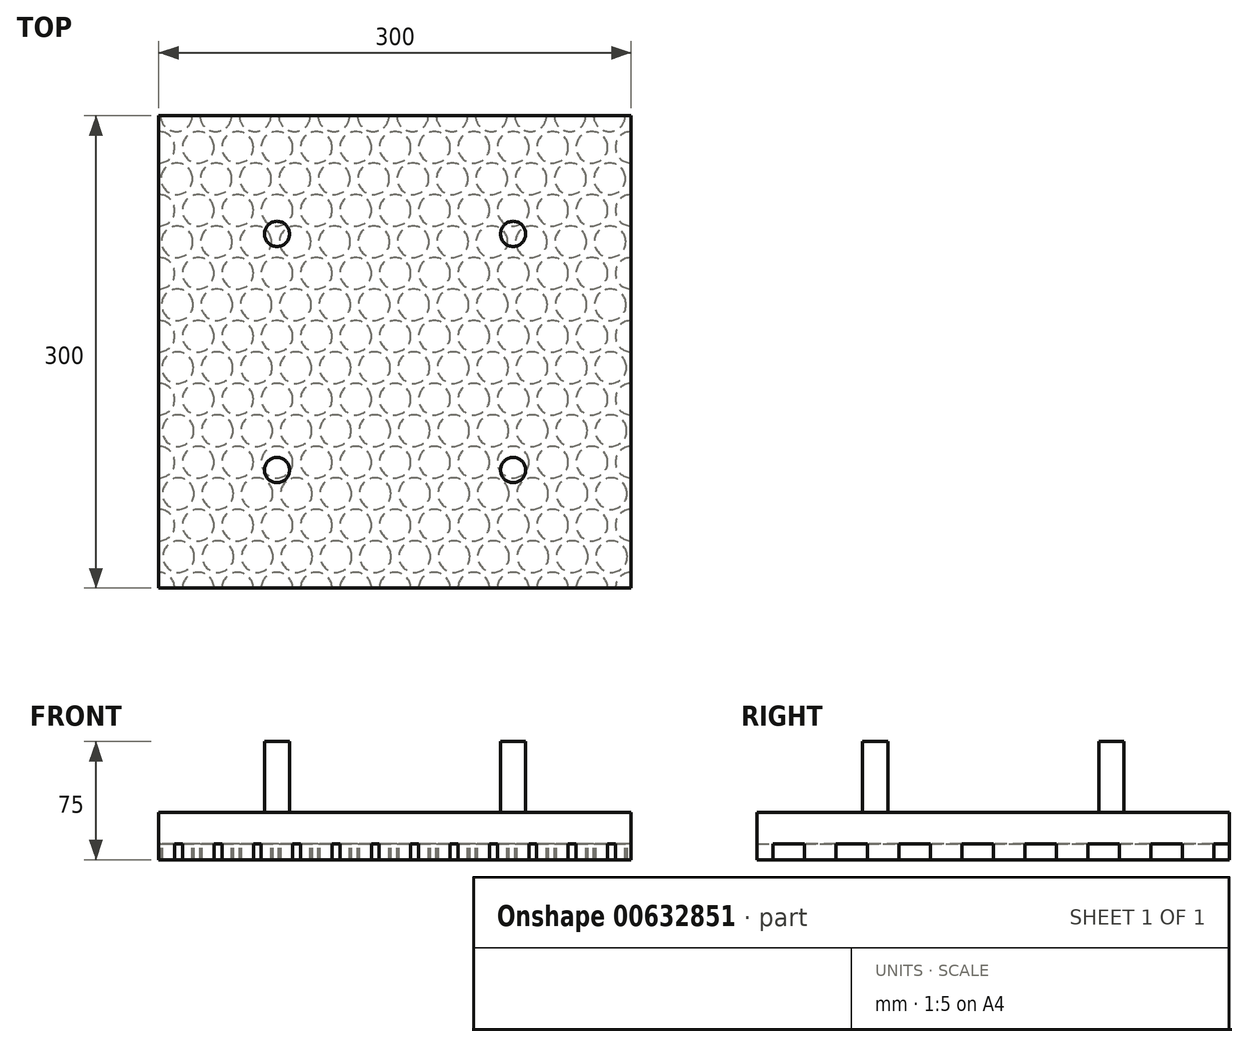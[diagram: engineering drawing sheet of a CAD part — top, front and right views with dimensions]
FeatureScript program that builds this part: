
annotation { "Feature Type Name" : "Feature", "Feature Type Description" : "" }
export const myFeature = defineFeature(function(context is Context, id is Id, definition is map)
    precondition{}
    {
        {
            var Q0;
            Q0=qCreatedBy(makeId("Top.planeOp"),FACE);
            var sketch = newSketch(context, id + "F0", { "sketchPlane" : qUnion([Q0])});
            skLineSegment(sketch, "E0.bottom", {"start": v(150, 150) * mm, "end": v(-150, 150) * mm});
            skLineSegment(sketch, "E0.top", {"start": v(150, -150) * mm, "end": v(-150, -150) * mm});
            skLineSegment(sketch, "E0.left", {"start": v(150, 150) * mm, "end": v(150, -150) * mm});
            skLineSegment(sketch, "E0.right", {"start": v(-150, 150) * mm, "end": v(-150, -150) * mm});
            skPoint(sketch, "E0.middle", {"position": v(0, 0) * mm});
            skSolve(sketch);
        }
        {
            var Q0;
            Q0 = qSketchRegion(id + "F0", true);
            extrude(context, id + "F1", {"entities" : qUnion([Q0]), "oppositeDirection" : true, "depth" : 20 * mm, "offsetDistance" : 25 * mm});
        }
        {
            var Q0;
            Q0=makeQuery(id+"F1.opExtrude","CAP_FACE",FACE,{"disambiguationData":[OSD([sQuery(id+"F0.wireOp",EDGE,"E0.bottom"),sQuery(id+"F0.wireOp",EDGE,"E0.top"),sQuery(id+"F0.wireOp",EDGE,"E0.left"),sQuery(id+"F0.wireOp",EDGE,"E0.right"),sQuery(id+"F0.wireOp",EDGE,"dzeue0mq-ryTN-MEcJ-6Cr2-TIuR5wwS6aSh"),sQuery(id+"F0.wireOp",EDGE,"DPBKmNIL-XfQO-MkqB-CjDe-bxSWGcwg6vfk"),sQuery(id+"F0.wireOp",EDGE,"v2nlQ9jK-8eDu-H6yK-LcaL-di8VHofIcNa3"),sQuery(id+"F0.wireOp",EDGE,"Z1CVN7Bm-QXrQ-2ffn-gUqZ-VcZKbfZv5ewL")])],"isStart":true});
            var sketch = newSketch(context, id + "F2", { "sketchPlane" : qUnion([Q0])});
            skCircle(sketch, "E1", {"center": v(-75, 75) * mm, "radius": 8 * mm});
            skCircle(sketch, "E2", {"center": v(75, 75) * mm, "radius": 8 * mm});
            skCircle(sketch, "E3", {"center": v(-75, -75) * mm, "radius": 8 * mm});
            skCircle(sketch, "E4", {"center": v(75, -75) * mm, "radius": 8 * mm});
            skSolve(sketch);
        }
        {
            var Q0;
            Q0 = qSketchRegion(id + "F2", true);
            extrude(context, id + "F3", {"entities" : qUnion([Q0]), "operationType" : NewBodyOperationType.ADD, "depth" : 45 * mm, "offsetDistance" : 25 * mm});
        }
        {
            var Q0;
            Q0=makeQuery(id+"F1.opExtrude","CAP_FACE",FACE,{"disambiguationData":[OSD([sQuery(id+"F0.wireOp",EDGE,"E0.bottom"),sQuery(id+"F0.wireOp",EDGE,"E0.top"),sQuery(id+"F0.wireOp",EDGE,"E0.left"),sQuery(id+"F0.wireOp",EDGE,"E0.right")])],"isStart":false});
            var sketch = newSketch(context, id + "F4", { "sketchPlane" : qUnion([Q0])});
            skCircle(sketch, "E5", {"center": v(-150, 150) * mm, "radius": 10 * mm});
            skCircle(sketch, "E6", {"center": v(-137.5, 130) * mm, "radius": 10 * mm});
            skCircle(sketch, "E7.0.1.0", {"center": v(-150, 110) * mm, "radius": 10 * mm});
            skCircle(sketch, "E7.0.2.0", {"center": v(-150, 70) * mm, "radius": 10 * mm});
            skCircle(sketch, "E7.0.3.0", {"center": v(-150, 30) * mm, "radius": 10 * mm});
            skCircle(sketch, "E7.0.4.0", {"center": v(-150, -10) * mm, "radius": 10 * mm});
            skCircle(sketch, "E7.0.5.0", {"center": v(-150, -50) * mm, "radius": 10 * mm});
            skCircle(sketch, "E7.0.6.0", {"center": v(-150, -90) * mm, "radius": 10 * mm});
            skCircle(sketch, "E7.1.0.0", {"center": v(-125, 150) * mm, "radius": 10 * mm});
            skCircle(sketch, "E7.1.1.0", {"center": v(-125, 110) * mm, "radius": 10 * mm});
            skCircle(sketch, "E7.1.2.0", {"center": v(-125, 70) * mm, "radius": 10 * mm});
            skCircle(sketch, "E7.1.3.0", {"center": v(-125, 30) * mm, "radius": 10 * mm});
            skCircle(sketch, "E7.1.4.0", {"center": v(-125, -10) * mm, "radius": 10 * mm});
            skCircle(sketch, "E7.1.5.0", {"center": v(-125, -50) * mm, "radius": 10 * mm});
            skCircle(sketch, "E7.1.6.0", {"center": v(-125, -90) * mm, "radius": 10 * mm});
            skCircle(sketch, "E7.2.0.0", {"center": v(-100, 150) * mm, "radius": 10 * mm});
            skCircle(sketch, "E7.2.1.0", {"center": v(-100, 110) * mm, "radius": 10 * mm});
            skCircle(sketch, "E7.2.2.0", {"center": v(-100, 70) * mm, "radius": 10 * mm});
            skCircle(sketch, "E7.2.3.0", {"center": v(-100, 30) * mm, "radius": 10 * mm});
            skCircle(sketch, "E7.2.4.0", {"center": v(-100, -10) * mm, "radius": 10 * mm});
            skCircle(sketch, "E7.2.5.0", {"center": v(-100, -50) * mm, "radius": 10 * mm});
            skCircle(sketch, "E7.2.6.0", {"center": v(-100, -90) * mm, "radius": 10 * mm});
            skCircle(sketch, "E7.3.0.0", {"center": v(-75, 150) * mm, "radius": 10 * mm});
            skCircle(sketch, "E7.3.1.0", {"center": v(-75, 110) * mm, "radius": 10 * mm});
            skCircle(sketch, "E7.3.2.0", {"center": v(-75, 70) * mm, "radius": 10 * mm});
            skCircle(sketch, "E7.3.3.0", {"center": v(-75, 30) * mm, "radius": 10 * mm});
            skCircle(sketch, "E7.3.4.0", {"center": v(-75, -10) * mm, "radius": 10 * mm});
            skCircle(sketch, "E7.3.5.0", {"center": v(-75, -50) * mm, "radius": 10 * mm});
            skCircle(sketch, "E7.3.6.0", {"center": v(-75, -90) * mm, "radius": 10 * mm});
            skCircle(sketch, "E7.4.0.0", {"center": v(-50, 150) * mm, "radius": 10 * mm});
            skCircle(sketch, "E7.4.1.0", {"center": v(-50, 110) * mm, "radius": 10 * mm});
            skCircle(sketch, "E7.4.2.0", {"center": v(-50, 70) * mm, "radius": 10 * mm});
            skCircle(sketch, "E7.4.3.0", {"center": v(-50, 30) * mm, "radius": 10 * mm});
            skCircle(sketch, "E7.4.4.0", {"center": v(-50, -10) * mm, "radius": 10 * mm});
            skCircle(sketch, "E7.4.5.0", {"center": v(-50, -50) * mm, "radius": 10 * mm});
            skCircle(sketch, "E7.4.6.0", {"center": v(-50, -90) * mm, "radius": 10 * mm});
            skCircle(sketch, "E7.5.0.0", {"center": v(-25, 150) * mm, "radius": 10 * mm});
            skCircle(sketch, "E7.5.1.0", {"center": v(-25, 110) * mm, "radius": 10 * mm});
            skCircle(sketch, "E7.5.2.0", {"center": v(-25, 70) * mm, "radius": 10 * mm});
            skCircle(sketch, "E7.5.3.0", {"center": v(-25, 30) * mm, "radius": 10 * mm});
            skCircle(sketch, "E7.5.4.0", {"center": v(-25, -10) * mm, "radius": 10 * mm});
            skCircle(sketch, "E7.5.5.0", {"center": v(-25, -50) * mm, "radius": 10 * mm});
            skCircle(sketch, "E7.5.6.0", {"center": v(-25, -90) * mm, "radius": 10 * mm});
            skCircle(sketch, "E7.6.0.0", {"center": v(0, 150) * mm, "radius": 10 * mm});
            skCircle(sketch, "E7.6.1.0", {"center": v(0, 110) * mm, "radius": 10 * mm});
            skCircle(sketch, "E7.6.2.0", {"center": v(0, 70) * mm, "radius": 10 * mm});
            skCircle(sketch, "E7.6.3.0", {"center": v(0, 30) * mm, "radius": 10 * mm});
            skCircle(sketch, "E7.6.4.0", {"center": v(0, -10) * mm, "radius": 10 * mm});
            skCircle(sketch, "E7.6.5.0", {"center": v(0, -50) * mm, "radius": 10 * mm});
            skCircle(sketch, "E7.6.6.0", {"center": v(0, -90) * mm, "radius": 10 * mm});
            skCircle(sketch, "E7.7.0.0", {"center": v(25, 150) * mm, "radius": 10 * mm});
            skCircle(sketch, "E7.7.1.0", {"center": v(25, 110) * mm, "radius": 10 * mm});
            skCircle(sketch, "E7.7.2.0", {"center": v(25, 70) * mm, "radius": 10 * mm});
            skCircle(sketch, "E7.7.3.0", {"center": v(25, 30) * mm, "radius": 10 * mm});
            skCircle(sketch, "E7.7.4.0", {"center": v(25, -10) * mm, "radius": 10 * mm});
            skCircle(sketch, "E7.7.5.0", {"center": v(25, -50) * mm, "radius": 10 * mm});
            skCircle(sketch, "E7.7.6.0", {"center": v(25, -90) * mm, "radius": 10 * mm});
            skCircle(sketch, "E7.8.0.0", {"center": v(50, 150) * mm, "radius": 10 * mm});
            skCircle(sketch, "E7.8.1.0", {"center": v(50, 110) * mm, "radius": 10 * mm});
            skCircle(sketch, "E7.8.2.0", {"center": v(50, 70) * mm, "radius": 10 * mm});
            skCircle(sketch, "E7.8.3.0", {"center": v(50, 30) * mm, "radius": 10 * mm});
            skCircle(sketch, "E7.8.4.0", {"center": v(50, -10) * mm, "radius": 10 * mm});
            skCircle(sketch, "E7.8.5.0", {"center": v(50, -50) * mm, "radius": 10 * mm});
            skCircle(sketch, "E7.8.6.0", {"center": v(50, -90) * mm, "radius": 10 * mm});
            skCircle(sketch, "E7.9.0.0", {"center": v(75, 150) * mm, "radius": 10 * mm});
            skCircle(sketch, "E7.9.1.0", {"center": v(75, 110) * mm, "radius": 10 * mm});
            skCircle(sketch, "E7.9.2.0", {"center": v(75, 70) * mm, "radius": 10 * mm});
            skCircle(sketch, "E7.9.3.0", {"center": v(75, 30) * mm, "radius": 10 * mm});
            skCircle(sketch, "E7.9.4.0", {"center": v(75, -10) * mm, "radius": 10 * mm});
            skCircle(sketch, "E7.9.5.0", {"center": v(75, -50) * mm, "radius": 10 * mm});
            skCircle(sketch, "E7.9.6.0", {"center": v(75, -90) * mm, "radius": 10 * mm});
            skLineSegment(sketch, "E7.direction1", {"start": v(-150, 150) * mm, "end": v(-125, 150) * mm, "construction": true});
            skLineSegment(sketch, "E7.direction2", {"start": v(-150, 150) * mm, "end": v(-150, 110) * mm, "construction": true});
            skCircle(sketch, "E8.0.1.0", {"center": v(-137.7, 90) * mm, "radius": 10 * mm});
            skCircle(sketch, "E8.0.2.0", {"center": v(-137.88, 50) * mm, "radius": 10 * mm});
            skCircle(sketch, "E8.0.3.0", {"center": v(-138.07, 10) * mm, "radius": 10 * mm});
            skCircle(sketch, "E8.0.4.0", {"center": v(-138.27, -30) * mm, "radius": 10 * mm});
            skCircle(sketch, "E8.0.5.0", {"center": v(-138.46, -70) * mm, "radius": 10 * mm});
            skCircle(sketch, "E8.0.6.0", {"center": v(-138.65, -110) * mm, "radius": 10 * mm});
            skCircle(sketch, "E8.0.7.0", {"center": v(-138.84, -150) * mm, "radius": 10 * mm});
            skCircle(sketch, "E8.1.0.0", {"center": v(-112.5, 130) * mm, "radius": 10 * mm});
            skCircle(sketch, "E8.1.1.0", {"center": v(-112.7, 90) * mm, "radius": 10 * mm});
            skCircle(sketch, "E8.1.2.0", {"center": v(-112.88, 50) * mm, "radius": 10 * mm});
            skCircle(sketch, "E8.1.3.0", {"center": v(-113.07, 10) * mm, "radius": 10 * mm});
            skCircle(sketch, "E8.1.4.0", {"center": v(-113.27, -30) * mm, "radius": 10 * mm});
            skCircle(sketch, "E8.1.5.0", {"center": v(-113.46, -70) * mm, "radius": 10 * mm});
            skCircle(sketch, "E8.1.6.0", {"center": v(-113.65, -110) * mm, "radius": 10 * mm});
            skCircle(sketch, "E8.1.7.0", {"center": v(-113.84, -150) * mm, "radius": 10 * mm});
            skCircle(sketch, "E8.2.0.0", {"center": v(-87.5, 130) * mm, "radius": 10 * mm});
            skCircle(sketch, "E8.2.1.0", {"center": v(-87.7, 90) * mm, "radius": 10 * mm});
            skCircle(sketch, "E8.2.2.0", {"center": v(-87.88, 50) * mm, "radius": 10 * mm});
            skCircle(sketch, "E8.2.3.0", {"center": v(-88.07, 10) * mm, "radius": 10 * mm});
            skCircle(sketch, "E8.2.4.0", {"center": v(-88.27, -30) * mm, "radius": 10 * mm});
            skCircle(sketch, "E8.2.5.0", {"center": v(-88.46, -70) * mm, "radius": 10 * mm});
            skCircle(sketch, "E8.2.6.0", {"center": v(-88.65, -110) * mm, "radius": 10 * mm});
            skCircle(sketch, "E8.2.7.0", {"center": v(-88.84, -150) * mm, "radius": 10 * mm});
            skCircle(sketch, "E8.3.0.0", {"center": v(-62.5, 130) * mm, "radius": 10 * mm});
            skCircle(sketch, "E8.3.1.0", {"center": v(-62.7, 90) * mm, "radius": 10 * mm});
            skCircle(sketch, "E8.3.2.0", {"center": v(-62.88, 50) * mm, "radius": 10 * mm});
            skCircle(sketch, "E8.3.3.0", {"center": v(-63.07, 10) * mm, "radius": 10 * mm});
            skCircle(sketch, "E8.3.4.0", {"center": v(-63.27, -30) * mm, "radius": 10 * mm});
            skCircle(sketch, "E8.3.5.0", {"center": v(-63.46, -70) * mm, "radius": 10 * mm});
            skCircle(sketch, "E8.3.6.0", {"center": v(-63.65, -110) * mm, "radius": 10 * mm});
            skCircle(sketch, "E8.3.7.0", {"center": v(-63.84, -150) * mm, "radius": 10 * mm});
            skCircle(sketch, "E8.4.0.0", {"center": v(-37.5, 130) * mm, "radius": 10 * mm});
            skCircle(sketch, "E8.4.1.0", {"center": v(-37.7, 90) * mm, "radius": 10 * mm});
            skCircle(sketch, "E8.4.2.0", {"center": v(-37.88, 50) * mm, "radius": 10 * mm});
            skCircle(sketch, "E8.4.3.0", {"center": v(-38.07, 10) * mm, "radius": 10 * mm});
            skCircle(sketch, "E8.4.4.0", {"center": v(-38.27, -30) * mm, "radius": 10 * mm});
            skCircle(sketch, "E8.4.5.0", {"center": v(-38.46, -70) * mm, "radius": 10 * mm});
            skCircle(sketch, "E8.4.6.0", {"center": v(-38.65, -110) * mm, "radius": 10 * mm});
            skCircle(sketch, "E8.4.7.0", {"center": v(-38.84, -150) * mm, "radius": 10 * mm});
            skCircle(sketch, "E8.5.0.0", {"center": v(-12.5, 130) * mm, "radius": 10 * mm});
            skCircle(sketch, "E8.5.1.0", {"center": v(-12.7, 90) * mm, "radius": 10 * mm});
            skCircle(sketch, "E8.5.2.0", {"center": v(-12.88, 50) * mm, "radius": 10 * mm});
            skCircle(sketch, "E8.5.3.0", {"center": v(-13.07, 10) * mm, "radius": 10 * mm});
            skCircle(sketch, "E8.5.4.0", {"center": v(-13.27, -30) * mm, "radius": 10 * mm});
            skCircle(sketch, "E8.5.5.0", {"center": v(-13.46, -70) * mm, "radius": 10 * mm});
            skCircle(sketch, "E8.5.6.0", {"center": v(-13.65, -110) * mm, "radius": 10 * mm});
            skCircle(sketch, "E8.5.7.0", {"center": v(-13.84, -150) * mm, "radius": 10 * mm});
            skCircle(sketch, "E8.6.0.0", {"center": v(12.5, 130) * mm, "radius": 10 * mm});
            skCircle(sketch, "E8.6.1.0", {"center": v(12.3, 90) * mm, "radius": 10 * mm});
            skCircle(sketch, "E8.6.2.0", {"center": v(12.12, 50) * mm, "radius": 10 * mm});
            skCircle(sketch, "E8.6.3.0", {"center": v(11.93, 10) * mm, "radius": 10 * mm});
            skCircle(sketch, "E8.6.4.0", {"center": v(11.73, -30) * mm, "radius": 10 * mm});
            skCircle(sketch, "E8.6.5.0", {"center": v(11.54, -70) * mm, "radius": 10 * mm});
            skCircle(sketch, "E8.6.6.0", {"center": v(11.35, -110) * mm, "radius": 10 * mm});
            skCircle(sketch, "E8.6.7.0", {"center": v(11.16, -150) * mm, "radius": 10 * mm});
            skCircle(sketch, "E8.7.0.0", {"center": v(37.5, 130) * mm, "radius": 10 * mm});
            skCircle(sketch, "E8.7.1.0", {"center": v(37.3, 90) * mm, "radius": 10 * mm});
            skCircle(sketch, "E8.7.2.0", {"center": v(37.12, 50) * mm, "radius": 10 * mm});
            skCircle(sketch, "E8.7.3.0", {"center": v(36.93, 10) * mm, "radius": 10 * mm});
            skCircle(sketch, "E8.7.4.0", {"center": v(36.73, -30) * mm, "radius": 10 * mm});
            skCircle(sketch, "E8.7.5.0", {"center": v(36.54, -70) * mm, "radius": 10 * mm});
            skCircle(sketch, "E8.7.6.0", {"center": v(36.35, -110) * mm, "radius": 10 * mm});
            skCircle(sketch, "E8.7.7.0", {"center": v(36.16, -150) * mm, "radius": 10 * mm});
            skCircle(sketch, "E8.8.0.0", {"center": v(62.5, 130) * mm, "radius": 10 * mm});
            skCircle(sketch, "E8.8.1.0", {"center": v(62.3, 90) * mm, "radius": 10 * mm});
            skCircle(sketch, "E8.8.2.0", {"center": v(62.12, 50) * mm, "radius": 10 * mm});
            skCircle(sketch, "E8.8.3.0", {"center": v(61.93, 10) * mm, "radius": 10 * mm});
            skCircle(sketch, "E8.8.4.0", {"center": v(61.73, -30) * mm, "radius": 10 * mm});
            skCircle(sketch, "E8.8.5.0", {"center": v(61.54, -70) * mm, "radius": 10 * mm});
            skCircle(sketch, "E8.8.6.0", {"center": v(61.35, -110) * mm, "radius": 10 * mm});
            skCircle(sketch, "E8.8.7.0", {"center": v(61.16, -150) * mm, "radius": 10 * mm});
            skCircle(sketch, "E8.9.0.0", {"center": v(87.5, 130) * mm, "radius": 10 * mm});
            skCircle(sketch, "E8.9.1.0", {"center": v(87.3, 90) * mm, "radius": 10 * mm});
            skCircle(sketch, "E8.9.2.0", {"center": v(87.12, 50) * mm, "radius": 10 * mm});
            skCircle(sketch, "E8.9.3.0", {"center": v(86.93, 10) * mm, "radius": 10 * mm});
            skCircle(sketch, "E8.9.4.0", {"center": v(86.73, -30) * mm, "radius": 10 * mm});
            skCircle(sketch, "E8.9.5.0", {"center": v(86.54, -70) * mm, "radius": 10 * mm});
            skCircle(sketch, "E8.9.6.0", {"center": v(86.35, -110) * mm, "radius": 10 * mm});
            skCircle(sketch, "E8.9.7.0", {"center": v(86.16, -150) * mm, "radius": 10 * mm});
            skCircle(sketch, "E8.10.0.0", {"center": v(112.5, 130) * mm, "radius": 10 * mm});
            skCircle(sketch, "E8.10.1.0", {"center": v(112.3, 90) * mm, "radius": 10 * mm});
            skCircle(sketch, "E8.10.2.0", {"center": v(112.12, 50) * mm, "radius": 10 * mm});
            skCircle(sketch, "E8.10.3.0", {"center": v(111.93, 10) * mm, "radius": 10 * mm});
            skCircle(sketch, "E8.10.4.0", {"center": v(111.73, -30) * mm, "radius": 10 * mm});
            skCircle(sketch, "E8.10.5.0", {"center": v(111.54, -70) * mm, "radius": 10 * mm});
            skCircle(sketch, "E8.10.6.0", {"center": v(111.35, -110) * mm, "radius": 10 * mm});
            skCircle(sketch, "E8.10.7.0", {"center": v(111.16, -150) * mm, "radius": 10 * mm});
            skCircle(sketch, "E8.11.0.0", {"center": v(137.5, 130) * mm, "radius": 10 * mm});
            skCircle(sketch, "E8.11.1.0", {"center": v(137.3, 90) * mm, "radius": 10 * mm});
            skCircle(sketch, "E8.11.2.0", {"center": v(137.12, 50) * mm, "radius": 10 * mm});
            skCircle(sketch, "E8.11.3.0", {"center": v(136.93, 10) * mm, "radius": 10 * mm});
            skCircle(sketch, "E8.11.4.0", {"center": v(136.73, -30) * mm, "radius": 10 * mm});
            skCircle(sketch, "E8.11.5.0", {"center": v(136.54, -70) * mm, "radius": 10 * mm});
            skCircle(sketch, "E8.11.6.0", {"center": v(136.35, -110) * mm, "radius": 10 * mm});
            skCircle(sketch, "E8.11.7.0", {"center": v(136.16, -150) * mm, "radius": 10 * mm});
            skLineSegment(sketch, "E8.direction1", {"start": v(-137.5, 130) * mm, "end": v(-112.5, 130) * mm, "construction": true});
            skLineSegment(sketch, "E8.direction2", {"start": v(-137.5, 130) * mm, "end": v(-137.7, 90) * mm, "construction": true});
            skCircle(sketch, "E9.0.0.7", {"center": v(-150, -130) * mm, "radius": 10 * mm});
            skCircle(sketch, "E9.0.1.7", {"center": v(-125, -130) * mm, "radius": 10 * mm});
            skCircle(sketch, "E9.0.2.7", {"center": v(-100, -130) * mm, "radius": 10 * mm});
            skCircle(sketch, "E9.0.3.7", {"center": v(-75, -130) * mm, "radius": 10 * mm});
            skCircle(sketch, "E9.0.4.7", {"center": v(-50, -130) * mm, "radius": 10 * mm});
            skCircle(sketch, "E9.0.5.7", {"center": v(-25, -130) * mm, "radius": 10 * mm});
            skCircle(sketch, "E9.0.6.7", {"center": v(0, -130) * mm, "radius": 10 * mm});
            skCircle(sketch, "E9.0.7.7", {"center": v(25, -130) * mm, "radius": 10 * mm});
            skCircle(sketch, "E9.0.8.7", {"center": v(50, -130) * mm, "radius": 10 * mm});
            skCircle(sketch, "E9.0.9.7", {"center": v(75, -130) * mm, "radius": 10 * mm});
            skCircle(sketch, "E10.0.10.0", {"center": v(100, 150) * mm, "radius": 10 * mm});
            skCircle(sketch, "E10.0.10.1", {"center": v(100, 110) * mm, "radius": 10 * mm});
            skCircle(sketch, "E10.0.10.2", {"center": v(100, 70) * mm, "radius": 10 * mm});
            skCircle(sketch, "E10.0.10.3", {"center": v(100, 30) * mm, "radius": 10 * mm});
            skCircle(sketch, "E10.0.10.4", {"center": v(100, -10) * mm, "radius": 10 * mm});
            skCircle(sketch, "E10.0.10.5", {"center": v(100, -50) * mm, "radius": 10 * mm});
            skCircle(sketch, "E10.0.10.6", {"center": v(100, -90) * mm, "radius": 10 * mm});
            skCircle(sketch, "E10.0.10.7", {"center": v(100, -130) * mm, "radius": 10 * mm});
            skCircle(sketch, "E10.0.11.0", {"center": v(125, 150) * mm, "radius": 10 * mm});
            skCircle(sketch, "E10.0.11.1", {"center": v(125, 110) * mm, "radius": 10 * mm});
            skCircle(sketch, "E10.0.11.2", {"center": v(125, 70) * mm, "radius": 10 * mm});
            skCircle(sketch, "E10.0.11.3", {"center": v(125, 30) * mm, "radius": 10 * mm});
            skCircle(sketch, "E10.0.11.4", {"center": v(125, -10) * mm, "radius": 10 * mm});
            skCircle(sketch, "E10.0.11.5", {"center": v(125, -50) * mm, "radius": 10 * mm});
            skCircle(sketch, "E10.0.11.6", {"center": v(125, -90) * mm, "radius": 10 * mm});
            skCircle(sketch, "E10.0.11.7", {"center": v(125, -130) * mm, "radius": 10 * mm});
            skCircle(sketch, "E11.0.12.0", {"center": v(150, 150) * mm, "radius": 10 * mm});
            skCircle(sketch, "E11.0.12.1", {"center": v(150, 110) * mm, "radius": 10 * mm});
            skCircle(sketch, "E11.0.12.2", {"center": v(150, 70) * mm, "radius": 10 * mm});
            skCircle(sketch, "E11.0.12.3", {"center": v(150, 30) * mm, "radius": 10 * mm});
            skCircle(sketch, "E11.0.12.4", {"center": v(150, -10) * mm, "radius": 10 * mm});
            skCircle(sketch, "E11.0.12.5", {"center": v(150, -50) * mm, "radius": 10 * mm});
            skCircle(sketch, "E11.0.12.6", {"center": v(150, -90) * mm, "radius": 10 * mm});
            skCircle(sketch, "E11.0.12.7", {"center": v(150, -130) * mm, "radius": 10 * mm});
            skSolve(sketch);
        }
        {
            var Q0;
            Q0=makeQuery(id+"F4.imprint","IMPRINT",FACE,{"disambiguationData":[TD([[makeQuery(id+"F4.imprint","IMPRINT",EDGE,{"derivedFrom":sQuery(id+"F4.wireOp",EDGE,"E6")}),1.0]])]});
            var Q1;
            Q1=makeQuery(id+"F4.imprint","IMPRINT",FACE,{"disambiguationData":[TD([[makeQuery(id+"F4.imprint","IMPRINT",EDGE,{"derivedFrom":sQuery(id+"F4.wireOp",EDGE,"E7.1.1.0")}),1.0]])]});
            var Q2;
            Q2=makeQuery(id+"F4.imprint","IMPRINT",FACE,{"disambiguationData":[TD([[makeQuery(id+"F4.imprint","IMPRINT",EDGE,{"derivedFrom":sQuery(id+"F4.wireOp",EDGE,"E7.1.2.0")}),1.0]])]});
            var Q3;
            Q3=makeQuery(id+"F4.imprint","IMPRINT",FACE,{"disambiguationData":[TD([[makeQuery(id+"F4.imprint","IMPRINT",EDGE,{"derivedFrom":sQuery(id+"F4.wireOp",EDGE,"E7.1.3.0")}),1.0]])]});
            var Q4;
            Q4=makeQuery(id+"F4.imprint","IMPRINT",FACE,{"disambiguationData":[TD([[makeQuery(id+"F4.imprint","IMPRINT",EDGE,{"derivedFrom":sQuery(id+"F4.wireOp",EDGE,"E7.1.4.0")}),1.0]])]});
            var Q5;
            Q5=makeQuery(id+"F4.imprint","IMPRINT",FACE,{"disambiguationData":[TD([[makeQuery(id+"F4.imprint","IMPRINT",EDGE,{"derivedFrom":sQuery(id+"F4.wireOp",EDGE,"E7.1.5.0")}),1.0]])]});
            var Q6;
            Q6=makeQuery(id+"F4.imprint","IMPRINT",FACE,{"disambiguationData":[TD([[makeQuery(id+"F4.imprint","IMPRINT",EDGE,{"derivedFrom":sQuery(id+"F4.wireOp",EDGE,"E7.1.6.0")}),1.0]])]});
            var Q7;
            Q7=makeQuery(id+"F4.imprint","IMPRINT",FACE,{"disambiguationData":[TD([[makeQuery(id+"F4.imprint","IMPRINT",EDGE,{"derivedFrom":sQuery(id+"F4.wireOp",EDGE,"E7.2.1.0")}),1.0]])]});
            var Q8;
            Q8=makeQuery(id+"F4.imprint","IMPRINT",FACE,{"disambiguationData":[TD([[makeQuery(id+"F4.imprint","IMPRINT",EDGE,{"derivedFrom":sQuery(id+"F4.wireOp",EDGE,"E7.2.2.0")}),1.0]])]});
            var Q9;
            Q9=makeQuery(id+"F4.imprint","IMPRINT",FACE,{"disambiguationData":[TD([[makeQuery(id+"F4.imprint","IMPRINT",EDGE,{"derivedFrom":sQuery(id+"F4.wireOp",EDGE,"E7.2.3.0")}),1.0]])]});
            var Q10;
            Q10=makeQuery(id+"F4.imprint","IMPRINT",FACE,{"disambiguationData":[TD([[makeQuery(id+"F4.imprint","IMPRINT",EDGE,{"derivedFrom":sQuery(id+"F4.wireOp",EDGE,"E7.2.4.0")}),1.0]])]});
            var Q11;
            Q11=makeQuery(id+"F4.imprint","IMPRINT",FACE,{"disambiguationData":[TD([[makeQuery(id+"F4.imprint","IMPRINT",EDGE,{"derivedFrom":sQuery(id+"F4.wireOp",EDGE,"E7.2.5.0")}),1.0]])]});
            var Q12;
            Q12=makeQuery(id+"F4.imprint","IMPRINT",FACE,{"disambiguationData":[TD([[makeQuery(id+"F4.imprint","IMPRINT",EDGE,{"derivedFrom":sQuery(id+"F4.wireOp",EDGE,"E7.2.6.0")}),1.0]])]});
            var Q13;
            Q13=makeQuery(id+"F4.imprint","IMPRINT",FACE,{"disambiguationData":[TD([[makeQuery(id+"F4.imprint","IMPRINT",EDGE,{"derivedFrom":sQuery(id+"F4.wireOp",EDGE,"E7.3.1.0")}),1.0]])]});
            var Q14;
            Q14=makeQuery(id+"F4.imprint","IMPRINT",FACE,{"disambiguationData":[TD([[makeQuery(id+"F4.imprint","IMPRINT",EDGE,{"derivedFrom":sQuery(id+"F4.wireOp",EDGE,"E7.3.2.0")}),1.0]])]});
            var Q15;
            Q15=makeQuery(id+"F4.imprint","IMPRINT",FACE,{"disambiguationData":[TD([[makeQuery(id+"F4.imprint","IMPRINT",EDGE,{"derivedFrom":sQuery(id+"F4.wireOp",EDGE,"E7.3.3.0")}),1.0]])]});
            var Q16;
            Q16=makeQuery(id+"F4.imprint","IMPRINT",FACE,{"disambiguationData":[TD([[makeQuery(id+"F4.imprint","IMPRINT",EDGE,{"derivedFrom":sQuery(id+"F4.wireOp",EDGE,"E7.3.4.0")}),1.0]])]});
            var Q17;
            Q17=makeQuery(id+"F4.imprint","IMPRINT",FACE,{"disambiguationData":[TD([[makeQuery(id+"F4.imprint","IMPRINT",EDGE,{"derivedFrom":sQuery(id+"F4.wireOp",EDGE,"E7.3.5.0")}),1.0]])]});
            var Q18;
            Q18=makeQuery(id+"F4.imprint","IMPRINT",FACE,{"disambiguationData":[TD([[makeQuery(id+"F4.imprint","IMPRINT",EDGE,{"derivedFrom":sQuery(id+"F4.wireOp",EDGE,"E7.3.6.0")}),1.0]])]});
            var Q19;
            Q19=makeQuery(id+"F4.imprint","IMPRINT",FACE,{"disambiguationData":[TD([[makeQuery(id+"F4.imprint","IMPRINT",EDGE,{"derivedFrom":sQuery(id+"F4.wireOp",EDGE,"E7.4.1.0")}),1.0]])]});
            var Q20;
            Q20=makeQuery(id+"F4.imprint","IMPRINT",FACE,{"disambiguationData":[TD([[makeQuery(id+"F4.imprint","IMPRINT",EDGE,{"derivedFrom":sQuery(id+"F4.wireOp",EDGE,"E7.4.2.0")}),1.0]])]});
            var Q21;
            Q21=makeQuery(id+"F4.imprint","IMPRINT",FACE,{"disambiguationData":[TD([[makeQuery(id+"F4.imprint","IMPRINT",EDGE,{"derivedFrom":sQuery(id+"F4.wireOp",EDGE,"E7.4.3.0")}),1.0]])]});
            var Q22;
            Q22=makeQuery(id+"F4.imprint","IMPRINT",FACE,{"disambiguationData":[TD([[makeQuery(id+"F4.imprint","IMPRINT",EDGE,{"derivedFrom":sQuery(id+"F4.wireOp",EDGE,"E7.4.4.0")}),1.0]])]});
            var Q23;
            Q23=makeQuery(id+"F4.imprint","IMPRINT",FACE,{"disambiguationData":[TD([[makeQuery(id+"F4.imprint","IMPRINT",EDGE,{"derivedFrom":sQuery(id+"F4.wireOp",EDGE,"E7.4.5.0")}),1.0]])]});
            var Q24;
            Q24=makeQuery(id+"F4.imprint","IMPRINT",FACE,{"disambiguationData":[TD([[makeQuery(id+"F4.imprint","IMPRINT",EDGE,{"derivedFrom":sQuery(id+"F4.wireOp",EDGE,"E7.4.6.0")}),1.0]])]});
            var Q25;
            Q25=makeQuery(id+"F4.imprint","IMPRINT",FACE,{"disambiguationData":[TD([[makeQuery(id+"F4.imprint","IMPRINT",EDGE,{"derivedFrom":sQuery(id+"F4.wireOp",EDGE,"E7.5.1.0")}),1.0]])]});
            var Q26;
            Q26=makeQuery(id+"F4.imprint","IMPRINT",FACE,{"disambiguationData":[TD([[makeQuery(id+"F4.imprint","IMPRINT",EDGE,{"derivedFrom":sQuery(id+"F4.wireOp",EDGE,"E7.5.2.0")}),1.0]])]});
            var Q27;
            Q27=makeQuery(id+"F4.imprint","IMPRINT",FACE,{"disambiguationData":[TD([[makeQuery(id+"F4.imprint","IMPRINT",EDGE,{"derivedFrom":sQuery(id+"F4.wireOp",EDGE,"E7.5.3.0")}),1.0]])]});
            var Q28;
            Q28=makeQuery(id+"F4.imprint","IMPRINT",FACE,{"disambiguationData":[TD([[makeQuery(id+"F4.imprint","IMPRINT",EDGE,{"derivedFrom":sQuery(id+"F4.wireOp",EDGE,"E7.5.4.0")}),1.0]])]});
            var Q29;
            Q29=makeQuery(id+"F4.imprint","IMPRINT",FACE,{"disambiguationData":[TD([[makeQuery(id+"F4.imprint","IMPRINT",EDGE,{"derivedFrom":sQuery(id+"F4.wireOp",EDGE,"E7.5.5.0")}),1.0]])]});
            var Q30;
            Q30=makeQuery(id+"F4.imprint","IMPRINT",FACE,{"disambiguationData":[TD([[makeQuery(id+"F4.imprint","IMPRINT",EDGE,{"derivedFrom":sQuery(id+"F4.wireOp",EDGE,"E7.5.6.0")}),1.0]])]});
            var Q31;
            Q31=makeQuery(id+"F4.imprint","IMPRINT",FACE,{"disambiguationData":[TD([[makeQuery(id+"F4.imprint","IMPRINT",EDGE,{"derivedFrom":sQuery(id+"F4.wireOp",EDGE,"E7.6.1.0")}),1.0]])]});
            var Q32;
            Q32=makeQuery(id+"F4.imprint","IMPRINT",FACE,{"disambiguationData":[TD([[makeQuery(id+"F4.imprint","IMPRINT",EDGE,{"derivedFrom":sQuery(id+"F4.wireOp",EDGE,"E7.6.2.0")}),1.0]])]});
            var Q33;
            Q33=makeQuery(id+"F4.imprint","IMPRINT",FACE,{"disambiguationData":[TD([[makeQuery(id+"F4.imprint","IMPRINT",EDGE,{"derivedFrom":sQuery(id+"F4.wireOp",EDGE,"E7.6.3.0")}),1.0]])]});
            var Q34;
            Q34=makeQuery(id+"F4.imprint","IMPRINT",FACE,{"disambiguationData":[TD([[makeQuery(id+"F4.imprint","IMPRINT",EDGE,{"derivedFrom":sQuery(id+"F4.wireOp",EDGE,"E7.6.4.0")}),1.0]])]});
            var Q35;
            Q35=makeQuery(id+"F4.imprint","IMPRINT",FACE,{"disambiguationData":[TD([[makeQuery(id+"F4.imprint","IMPRINT",EDGE,{"derivedFrom":sQuery(id+"F4.wireOp",EDGE,"E7.6.5.0")}),1.0]])]});
            var Q36;
            Q36=makeQuery(id+"F4.imprint","IMPRINT",FACE,{"disambiguationData":[TD([[makeQuery(id+"F4.imprint","IMPRINT",EDGE,{"derivedFrom":sQuery(id+"F4.wireOp",EDGE,"E7.6.6.0")}),1.0]])]});
            var Q37;
            Q37=makeQuery(id+"F4.imprint","IMPRINT",FACE,{"disambiguationData":[TD([[makeQuery(id+"F4.imprint","IMPRINT",EDGE,{"derivedFrom":sQuery(id+"F4.wireOp",EDGE,"E7.7.1.0")}),1.0]])]});
            var Q38;
            Q38=makeQuery(id+"F4.imprint","IMPRINT",FACE,{"disambiguationData":[TD([[makeQuery(id+"F4.imprint","IMPRINT",EDGE,{"derivedFrom":sQuery(id+"F4.wireOp",EDGE,"E7.7.2.0")}),1.0]])]});
            var Q39;
            Q39=makeQuery(id+"F4.imprint","IMPRINT",FACE,{"disambiguationData":[TD([[makeQuery(id+"F4.imprint","IMPRINT",EDGE,{"derivedFrom":sQuery(id+"F4.wireOp",EDGE,"E7.7.3.0")}),1.0]])]});
            var Q40;
            Q40=makeQuery(id+"F4.imprint","IMPRINT",FACE,{"disambiguationData":[TD([[makeQuery(id+"F4.imprint","IMPRINT",EDGE,{"derivedFrom":sQuery(id+"F4.wireOp",EDGE,"E7.7.4.0")}),1.0]])]});
            var Q41;
            Q41=makeQuery(id+"F4.imprint","IMPRINT",FACE,{"disambiguationData":[TD([[makeQuery(id+"F4.imprint","IMPRINT",EDGE,{"derivedFrom":sQuery(id+"F4.wireOp",EDGE,"E7.7.5.0")}),1.0]])]});
            var Q42;
            Q42=makeQuery(id+"F4.imprint","IMPRINT",FACE,{"disambiguationData":[TD([[makeQuery(id+"F4.imprint","IMPRINT",EDGE,{"derivedFrom":sQuery(id+"F4.wireOp",EDGE,"E7.7.6.0")}),1.0]])]});
            var Q43;
            Q43=makeQuery(id+"F4.imprint","IMPRINT",FACE,{"disambiguationData":[TD([[makeQuery(id+"F4.imprint","IMPRINT",EDGE,{"derivedFrom":sQuery(id+"F4.wireOp",EDGE,"E7.8.1.0")}),1.0]])]});
            var Q44;
            Q44=makeQuery(id+"F4.imprint","IMPRINT",FACE,{"disambiguationData":[TD([[makeQuery(id+"F4.imprint","IMPRINT",EDGE,{"derivedFrom":sQuery(id+"F4.wireOp",EDGE,"E7.8.2.0")}),1.0]])]});
            var Q45;
            Q45=makeQuery(id+"F4.imprint","IMPRINT",FACE,{"disambiguationData":[TD([[makeQuery(id+"F4.imprint","IMPRINT",EDGE,{"derivedFrom":sQuery(id+"F4.wireOp",EDGE,"E7.8.3.0")}),1.0]])]});
            var Q46;
            Q46=makeQuery(id+"F4.imprint","IMPRINT",FACE,{"disambiguationData":[TD([[makeQuery(id+"F4.imprint","IMPRINT",EDGE,{"derivedFrom":sQuery(id+"F4.wireOp",EDGE,"E7.8.4.0")}),1.0]])]});
            var Q47;
            Q47=makeQuery(id+"F4.imprint","IMPRINT",FACE,{"disambiguationData":[TD([[makeQuery(id+"F4.imprint","IMPRINT",EDGE,{"derivedFrom":sQuery(id+"F4.wireOp",EDGE,"E7.8.5.0")}),1.0]])]});
            var Q48;
            Q48=makeQuery(id+"F4.imprint","IMPRINT",FACE,{"disambiguationData":[TD([[makeQuery(id+"F4.imprint","IMPRINT",EDGE,{"derivedFrom":sQuery(id+"F4.wireOp",EDGE,"E7.8.6.0")}),1.0]])]});
            var Q49;
            Q49=makeQuery(id+"F4.imprint","IMPRINT",FACE,{"disambiguationData":[TD([[makeQuery(id+"F4.imprint","IMPRINT",EDGE,{"derivedFrom":sQuery(id+"F4.wireOp",EDGE,"E7.9.1.0")}),1.0]])]});
            var Q50;
            Q50=makeQuery(id+"F4.imprint","IMPRINT",FACE,{"disambiguationData":[TD([[makeQuery(id+"F4.imprint","IMPRINT",EDGE,{"derivedFrom":sQuery(id+"F4.wireOp",EDGE,"E7.9.2.0")}),1.0]])]});
            var Q51;
            Q51=makeQuery(id+"F4.imprint","IMPRINT",FACE,{"disambiguationData":[TD([[makeQuery(id+"F4.imprint","IMPRINT",EDGE,{"derivedFrom":sQuery(id+"F4.wireOp",EDGE,"E7.9.3.0")}),1.0]])]});
            var Q52;
            Q52=makeQuery(id+"F4.imprint","IMPRINT",FACE,{"disambiguationData":[TD([[makeQuery(id+"F4.imprint","IMPRINT",EDGE,{"derivedFrom":sQuery(id+"F4.wireOp",EDGE,"E7.9.4.0")}),1.0]])]});
            var Q53;
            Q53=makeQuery(id+"F4.imprint","IMPRINT",FACE,{"disambiguationData":[TD([[makeQuery(id+"F4.imprint","IMPRINT",EDGE,{"derivedFrom":sQuery(id+"F4.wireOp",EDGE,"E7.9.5.0")}),1.0]])]});
            var Q54;
            Q54=makeQuery(id+"F4.imprint","IMPRINT",FACE,{"disambiguationData":[TD([[makeQuery(id+"F4.imprint","IMPRINT",EDGE,{"derivedFrom":sQuery(id+"F4.wireOp",EDGE,"E7.9.6.0")}),1.0]])]});
            var Q55;
            Q55=makeQuery(id+"F4.imprint","IMPRINT",FACE,{"disambiguationData":[TD([[makeQuery(id+"F4.imprint","IMPRINT",EDGE,{"derivedFrom":sQuery(id+"F4.wireOp",EDGE,"E8.0.1.0")}),1.0]])]});
            var Q56;
            Q56=makeQuery(id+"F4.imprint","IMPRINT",FACE,{"disambiguationData":[TD([[makeQuery(id+"F4.imprint","IMPRINT",EDGE,{"derivedFrom":sQuery(id+"F4.wireOp",EDGE,"E8.0.2.0")}),1.0]])]});
            var Q57;
            Q57=makeQuery(id+"F4.imprint","IMPRINT",FACE,{"disambiguationData":[TD([[makeQuery(id+"F4.imprint","IMPRINT",EDGE,{"derivedFrom":sQuery(id+"F4.wireOp",EDGE,"E8.0.3.0")}),1.0]])]});
            var Q58;
            Q58=makeQuery(id+"F4.imprint","IMPRINT",FACE,{"disambiguationData":[TD([[makeQuery(id+"F4.imprint","IMPRINT",EDGE,{"derivedFrom":sQuery(id+"F4.wireOp",EDGE,"E8.0.4.0")}),1.0]])]});
            var Q59;
            Q59=makeQuery(id+"F4.imprint","IMPRINT",FACE,{"disambiguationData":[TD([[makeQuery(id+"F4.imprint","IMPRINT",EDGE,{"derivedFrom":sQuery(id+"F4.wireOp",EDGE,"E8.0.5.0")}),1.0]])]});
            var Q60;
            Q60=makeQuery(id+"F4.imprint","IMPRINT",FACE,{"disambiguationData":[TD([[makeQuery(id+"F4.imprint","IMPRINT",EDGE,{"derivedFrom":sQuery(id+"F4.wireOp",EDGE,"E8.0.6.0")}),1.0]])]});
            var Q61;
            Q61=makeQuery(id+"F4.imprint","IMPRINT",FACE,{"disambiguationData":[TD([[makeQuery(id+"F4.imprint","IMPRINT",EDGE,{"derivedFrom":sQuery(id+"F4.wireOp",EDGE,"E8.1.0.0")}),1.0]])]});
            var Q62;
            Q62=makeQuery(id+"F4.imprint","IMPRINT",FACE,{"disambiguationData":[TD([[makeQuery(id+"F4.imprint","IMPRINT",EDGE,{"derivedFrom":sQuery(id+"F4.wireOp",EDGE,"E8.1.1.0")}),1.0]])]});
            var Q63;
            Q63=makeQuery(id+"F4.imprint","IMPRINT",FACE,{"disambiguationData":[TD([[makeQuery(id+"F4.imprint","IMPRINT",EDGE,{"derivedFrom":sQuery(id+"F4.wireOp",EDGE,"E8.1.2.0")}),1.0]])]});
            var Q64;
            Q64=makeQuery(id+"F4.imprint","IMPRINT",FACE,{"disambiguationData":[TD([[makeQuery(id+"F4.imprint","IMPRINT",EDGE,{"derivedFrom":sQuery(id+"F4.wireOp",EDGE,"E8.1.3.0")}),1.0]])]});
            var Q65;
            Q65=makeQuery(id+"F4.imprint","IMPRINT",FACE,{"disambiguationData":[TD([[makeQuery(id+"F4.imprint","IMPRINT",EDGE,{"derivedFrom":sQuery(id+"F4.wireOp",EDGE,"E8.1.4.0")}),1.0]])]});
            var Q66;
            Q66=makeQuery(id+"F4.imprint","IMPRINT",FACE,{"disambiguationData":[TD([[makeQuery(id+"F4.imprint","IMPRINT",EDGE,{"derivedFrom":sQuery(id+"F4.wireOp",EDGE,"E8.1.5.0")}),1.0]])]});
            var Q67;
            Q67=makeQuery(id+"F4.imprint","IMPRINT",FACE,{"disambiguationData":[TD([[makeQuery(id+"F4.imprint","IMPRINT",EDGE,{"derivedFrom":sQuery(id+"F4.wireOp",EDGE,"E8.1.6.0")}),1.0]])]});
            var Q68;
            Q68=makeQuery(id+"F4.imprint","IMPRINT",FACE,{"disambiguationData":[TD([[makeQuery(id+"F4.imprint","IMPRINT",EDGE,{"derivedFrom":sQuery(id+"F4.wireOp",EDGE,"E8.2.0.0")}),1.0]])]});
            var Q69;
            Q69=makeQuery(id+"F4.imprint","IMPRINT",FACE,{"disambiguationData":[TD([[makeQuery(id+"F4.imprint","IMPRINT",EDGE,{"derivedFrom":sQuery(id+"F4.wireOp",EDGE,"E8.2.1.0")}),1.0]])]});
            var Q70;
            Q70=makeQuery(id+"F4.imprint","IMPRINT",FACE,{"disambiguationData":[TD([[makeQuery(id+"F4.imprint","IMPRINT",EDGE,{"derivedFrom":sQuery(id+"F4.wireOp",EDGE,"E8.2.2.0")}),1.0]])]});
            var Q71;
            Q71=makeQuery(id+"F4.imprint","IMPRINT",FACE,{"disambiguationData":[TD([[makeQuery(id+"F4.imprint","IMPRINT",EDGE,{"derivedFrom":sQuery(id+"F4.wireOp",EDGE,"E8.2.3.0")}),1.0]])]});
            var Q72;
            Q72=makeQuery(id+"F4.imprint","IMPRINT",FACE,{"disambiguationData":[TD([[makeQuery(id+"F4.imprint","IMPRINT",EDGE,{"derivedFrom":sQuery(id+"F4.wireOp",EDGE,"E8.2.4.0")}),1.0]])]});
            var Q73;
            Q73=makeQuery(id+"F4.imprint","IMPRINT",FACE,{"disambiguationData":[TD([[makeQuery(id+"F4.imprint","IMPRINT",EDGE,{"derivedFrom":sQuery(id+"F4.wireOp",EDGE,"E8.2.5.0")}),1.0]])]});
            var Q74;
            Q74=makeQuery(id+"F4.imprint","IMPRINT",FACE,{"disambiguationData":[TD([[makeQuery(id+"F4.imprint","IMPRINT",EDGE,{"derivedFrom":sQuery(id+"F4.wireOp",EDGE,"E8.2.6.0")}),1.0]])]});
            var Q75;
            Q75=makeQuery(id+"F4.imprint","IMPRINT",FACE,{"disambiguationData":[TD([[makeQuery(id+"F4.imprint","IMPRINT",EDGE,{"derivedFrom":sQuery(id+"F4.wireOp",EDGE,"E8.3.0.0")}),1.0]])]});
            var Q76;
            Q76=makeQuery(id+"F4.imprint","IMPRINT",FACE,{"disambiguationData":[TD([[makeQuery(id+"F4.imprint","IMPRINT",EDGE,{"derivedFrom":sQuery(id+"F4.wireOp",EDGE,"E8.3.1.0")}),1.0]])]});
            var Q77;
            Q77=makeQuery(id+"F4.imprint","IMPRINT",FACE,{"disambiguationData":[TD([[makeQuery(id+"F4.imprint","IMPRINT",EDGE,{"derivedFrom":sQuery(id+"F4.wireOp",EDGE,"E8.3.2.0")}),1.0]])]});
            var Q78;
            Q78=makeQuery(id+"F4.imprint","IMPRINT",FACE,{"disambiguationData":[TD([[makeQuery(id+"F4.imprint","IMPRINT",EDGE,{"derivedFrom":sQuery(id+"F4.wireOp",EDGE,"E8.3.3.0")}),1.0]])]});
            var Q79;
            Q79=makeQuery(id+"F4.imprint","IMPRINT",FACE,{"disambiguationData":[TD([[makeQuery(id+"F4.imprint","IMPRINT",EDGE,{"derivedFrom":sQuery(id+"F4.wireOp",EDGE,"E8.3.4.0")}),1.0]])]});
            var Q80;
            Q80=makeQuery(id+"F4.imprint","IMPRINT",FACE,{"disambiguationData":[TD([[makeQuery(id+"F4.imprint","IMPRINT",EDGE,{"derivedFrom":sQuery(id+"F4.wireOp",EDGE,"E8.3.5.0")}),1.0]])]});
            var Q81;
            Q81=makeQuery(id+"F4.imprint","IMPRINT",FACE,{"disambiguationData":[TD([[makeQuery(id+"F4.imprint","IMPRINT",EDGE,{"derivedFrom":sQuery(id+"F4.wireOp",EDGE,"E8.3.6.0")}),1.0]])]});
            var Q82;
            Q82=makeQuery(id+"F4.imprint","IMPRINT",FACE,{"disambiguationData":[TD([[makeQuery(id+"F4.imprint","IMPRINT",EDGE,{"derivedFrom":sQuery(id+"F4.wireOp",EDGE,"E8.4.0.0")}),1.0]])]});
            var Q83;
            Q83=makeQuery(id+"F4.imprint","IMPRINT",FACE,{"disambiguationData":[TD([[makeQuery(id+"F4.imprint","IMPRINT",EDGE,{"derivedFrom":sQuery(id+"F4.wireOp",EDGE,"E8.4.1.0")}),1.0]])]});
            var Q84;
            Q84=makeQuery(id+"F4.imprint","IMPRINT",FACE,{"disambiguationData":[TD([[makeQuery(id+"F4.imprint","IMPRINT",EDGE,{"derivedFrom":sQuery(id+"F4.wireOp",EDGE,"E8.4.2.0")}),1.0]])]});
            var Q85;
            Q85=makeQuery(id+"F4.imprint","IMPRINT",FACE,{"disambiguationData":[TD([[makeQuery(id+"F4.imprint","IMPRINT",EDGE,{"derivedFrom":sQuery(id+"F4.wireOp",EDGE,"E8.4.3.0")}),1.0]])]});
            var Q86;
            Q86=makeQuery(id+"F4.imprint","IMPRINT",FACE,{"disambiguationData":[TD([[makeQuery(id+"F4.imprint","IMPRINT",EDGE,{"derivedFrom":sQuery(id+"F4.wireOp",EDGE,"E8.4.4.0")}),1.0]])]});
            var Q87;
            Q87=makeQuery(id+"F4.imprint","IMPRINT",FACE,{"disambiguationData":[TD([[makeQuery(id+"F4.imprint","IMPRINT",EDGE,{"derivedFrom":sQuery(id+"F4.wireOp",EDGE,"E8.4.5.0")}),1.0]])]});
            var Q88;
            Q88=makeQuery(id+"F4.imprint","IMPRINT",FACE,{"disambiguationData":[TD([[makeQuery(id+"F4.imprint","IMPRINT",EDGE,{"derivedFrom":sQuery(id+"F4.wireOp",EDGE,"E8.4.6.0")}),1.0]])]});
            var Q89;
            Q89=makeQuery(id+"F4.imprint","IMPRINT",FACE,{"disambiguationData":[TD([[makeQuery(id+"F4.imprint","IMPRINT",EDGE,{"derivedFrom":sQuery(id+"F4.wireOp",EDGE,"E8.5.0.0")}),1.0]])]});
            var Q90;
            Q90=makeQuery(id+"F4.imprint","IMPRINT",FACE,{"disambiguationData":[TD([[makeQuery(id+"F4.imprint","IMPRINT",EDGE,{"derivedFrom":sQuery(id+"F4.wireOp",EDGE,"E8.5.1.0")}),1.0]])]});
            var Q91;
            Q91=makeQuery(id+"F4.imprint","IMPRINT",FACE,{"disambiguationData":[TD([[makeQuery(id+"F4.imprint","IMPRINT",EDGE,{"derivedFrom":sQuery(id+"F4.wireOp",EDGE,"E8.5.2.0")}),1.0]])]});
            var Q92;
            Q92=makeQuery(id+"F4.imprint","IMPRINT",FACE,{"disambiguationData":[TD([[makeQuery(id+"F4.imprint","IMPRINT",EDGE,{"derivedFrom":sQuery(id+"F4.wireOp",EDGE,"E8.5.3.0")}),1.0]])]});
            var Q93;
            Q93=makeQuery(id+"F4.imprint","IMPRINT",FACE,{"disambiguationData":[TD([[makeQuery(id+"F4.imprint","IMPRINT",EDGE,{"derivedFrom":sQuery(id+"F4.wireOp",EDGE,"E8.5.4.0")}),1.0]])]});
            var Q94;
            Q94=makeQuery(id+"F4.imprint","IMPRINT",FACE,{"disambiguationData":[TD([[makeQuery(id+"F4.imprint","IMPRINT",EDGE,{"derivedFrom":sQuery(id+"F4.wireOp",EDGE,"E8.5.5.0")}),1.0]])]});
            var Q95;
            Q95=makeQuery(id+"F4.imprint","IMPRINT",FACE,{"disambiguationData":[TD([[makeQuery(id+"F4.imprint","IMPRINT",EDGE,{"derivedFrom":sQuery(id+"F4.wireOp",EDGE,"E8.5.6.0")}),1.0]])]});
            var Q96;
            Q96=makeQuery(id+"F4.imprint","IMPRINT",FACE,{"disambiguationData":[TD([[makeQuery(id+"F4.imprint","IMPRINT",EDGE,{"derivedFrom":sQuery(id+"F4.wireOp",EDGE,"E8.6.0.0")}),1.0]])]});
            var Q97;
            Q97=makeQuery(id+"F4.imprint","IMPRINT",FACE,{"disambiguationData":[TD([[makeQuery(id+"F4.imprint","IMPRINT",EDGE,{"derivedFrom":sQuery(id+"F4.wireOp",EDGE,"E8.6.1.0")}),1.0]])]});
            var Q98;
            Q98=makeQuery(id+"F4.imprint","IMPRINT",FACE,{"disambiguationData":[TD([[makeQuery(id+"F4.imprint","IMPRINT",EDGE,{"derivedFrom":sQuery(id+"F4.wireOp",EDGE,"E8.6.2.0")}),1.0]])]});
            var Q99;
            Q99=makeQuery(id+"F4.imprint","IMPRINT",FACE,{"disambiguationData":[TD([[makeQuery(id+"F4.imprint","IMPRINT",EDGE,{"derivedFrom":sQuery(id+"F4.wireOp",EDGE,"E8.6.3.0")}),1.0]])]});
            var Q100;
            Q100=makeQuery(id+"F4.imprint","IMPRINT",FACE,{"disambiguationData":[TD([[makeQuery(id+"F4.imprint","IMPRINT",EDGE,{"derivedFrom":sQuery(id+"F4.wireOp",EDGE,"E8.6.4.0")}),1.0]])]});
            var Q101;
            Q101=makeQuery(id+"F4.imprint","IMPRINT",FACE,{"disambiguationData":[TD([[makeQuery(id+"F4.imprint","IMPRINT",EDGE,{"derivedFrom":sQuery(id+"F4.wireOp",EDGE,"E8.6.5.0")}),1.0]])]});
            var Q102;
            Q102=makeQuery(id+"F4.imprint","IMPRINT",FACE,{"disambiguationData":[TD([[makeQuery(id+"F4.imprint","IMPRINT",EDGE,{"derivedFrom":sQuery(id+"F4.wireOp",EDGE,"E8.6.6.0")}),1.0]])]});
            var Q103;
            Q103=makeQuery(id+"F4.imprint","IMPRINT",FACE,{"disambiguationData":[TD([[makeQuery(id+"F4.imprint","IMPRINT",EDGE,{"derivedFrom":sQuery(id+"F4.wireOp",EDGE,"E8.7.0.0")}),1.0]])]});
            var Q104;
            Q104=makeQuery(id+"F4.imprint","IMPRINT",FACE,{"disambiguationData":[TD([[makeQuery(id+"F4.imprint","IMPRINT",EDGE,{"derivedFrom":sQuery(id+"F4.wireOp",EDGE,"E8.7.1.0")}),1.0]])]});
            var Q105;
            Q105=makeQuery(id+"F4.imprint","IMPRINT",FACE,{"disambiguationData":[TD([[makeQuery(id+"F4.imprint","IMPRINT",EDGE,{"derivedFrom":sQuery(id+"F4.wireOp",EDGE,"E8.7.2.0")}),1.0]])]});
            var Q106;
            Q106=makeQuery(id+"F4.imprint","IMPRINT",FACE,{"disambiguationData":[TD([[makeQuery(id+"F4.imprint","IMPRINT",EDGE,{"derivedFrom":sQuery(id+"F4.wireOp",EDGE,"E8.7.3.0")}),1.0]])]});
            var Q107;
            Q107=makeQuery(id+"F4.imprint","IMPRINT",FACE,{"disambiguationData":[TD([[makeQuery(id+"F4.imprint","IMPRINT",EDGE,{"derivedFrom":sQuery(id+"F4.wireOp",EDGE,"E8.7.4.0")}),1.0]])]});
            var Q108;
            Q108=makeQuery(id+"F4.imprint","IMPRINT",FACE,{"disambiguationData":[TD([[makeQuery(id+"F4.imprint","IMPRINT",EDGE,{"derivedFrom":sQuery(id+"F4.wireOp",EDGE,"E8.7.5.0")}),1.0]])]});
            var Q109;
            Q109=makeQuery(id+"F4.imprint","IMPRINT",FACE,{"disambiguationData":[TD([[makeQuery(id+"F4.imprint","IMPRINT",EDGE,{"derivedFrom":sQuery(id+"F4.wireOp",EDGE,"E8.7.6.0")}),1.0]])]});
            var Q110;
            Q110=makeQuery(id+"F4.imprint","IMPRINT",FACE,{"disambiguationData":[TD([[makeQuery(id+"F4.imprint","IMPRINT",EDGE,{"derivedFrom":sQuery(id+"F4.wireOp",EDGE,"E8.8.0.0")}),1.0]])]});
            var Q111;
            Q111=makeQuery(id+"F4.imprint","IMPRINT",FACE,{"disambiguationData":[TD([[makeQuery(id+"F4.imprint","IMPRINT",EDGE,{"derivedFrom":sQuery(id+"F4.wireOp",EDGE,"E8.8.1.0")}),1.0]])]});
            var Q112;
            Q112=makeQuery(id+"F4.imprint","IMPRINT",FACE,{"disambiguationData":[TD([[makeQuery(id+"F4.imprint","IMPRINT",EDGE,{"derivedFrom":sQuery(id+"F4.wireOp",EDGE,"E8.8.2.0")}),1.0]])]});
            var Q113;
            Q113=makeQuery(id+"F4.imprint","IMPRINT",FACE,{"disambiguationData":[TD([[makeQuery(id+"F4.imprint","IMPRINT",EDGE,{"derivedFrom":sQuery(id+"F4.wireOp",EDGE,"E8.8.3.0")}),1.0]])]});
            var Q114;
            Q114=makeQuery(id+"F4.imprint","IMPRINT",FACE,{"disambiguationData":[TD([[makeQuery(id+"F4.imprint","IMPRINT",EDGE,{"derivedFrom":sQuery(id+"F4.wireOp",EDGE,"E8.8.4.0")}),1.0]])]});
            var Q115;
            Q115=makeQuery(id+"F4.imprint","IMPRINT",FACE,{"disambiguationData":[TD([[makeQuery(id+"F4.imprint","IMPRINT",EDGE,{"derivedFrom":sQuery(id+"F4.wireOp",EDGE,"E8.8.5.0")}),1.0]])]});
            var Q116;
            Q116=makeQuery(id+"F4.imprint","IMPRINT",FACE,{"disambiguationData":[TD([[makeQuery(id+"F4.imprint","IMPRINT",EDGE,{"derivedFrom":sQuery(id+"F4.wireOp",EDGE,"E8.8.6.0")}),1.0]])]});
            var Q117;
            Q117=makeQuery(id+"F4.imprint","IMPRINT",FACE,{"disambiguationData":[TD([[makeQuery(id+"F4.imprint","IMPRINT",EDGE,{"derivedFrom":sQuery(id+"F4.wireOp",EDGE,"E8.9.0.0")}),1.0]])]});
            var Q118;
            Q118=makeQuery(id+"F4.imprint","IMPRINT",FACE,{"disambiguationData":[TD([[makeQuery(id+"F4.imprint","IMPRINT",EDGE,{"derivedFrom":sQuery(id+"F4.wireOp",EDGE,"E8.9.1.0")}),1.0]])]});
            var Q119;
            Q119=makeQuery(id+"F4.imprint","IMPRINT",FACE,{"disambiguationData":[TD([[makeQuery(id+"F4.imprint","IMPRINT",EDGE,{"derivedFrom":sQuery(id+"F4.wireOp",EDGE,"E8.9.2.0")}),1.0]])]});
            var Q120;
            Q120=makeQuery(id+"F4.imprint","IMPRINT",FACE,{"disambiguationData":[TD([[makeQuery(id+"F4.imprint","IMPRINT",EDGE,{"derivedFrom":sQuery(id+"F4.wireOp",EDGE,"E8.9.3.0")}),1.0]])]});
            var Q121;
            Q121=makeQuery(id+"F4.imprint","IMPRINT",FACE,{"disambiguationData":[TD([[makeQuery(id+"F4.imprint","IMPRINT",EDGE,{"derivedFrom":sQuery(id+"F4.wireOp",EDGE,"E8.9.4.0")}),1.0]])]});
            var Q122;
            Q122=makeQuery(id+"F4.imprint","IMPRINT",FACE,{"disambiguationData":[TD([[makeQuery(id+"F4.imprint","IMPRINT",EDGE,{"derivedFrom":sQuery(id+"F4.wireOp",EDGE,"E8.9.5.0")}),1.0]])]});
            var Q123;
            Q123=makeQuery(id+"F4.imprint","IMPRINT",FACE,{"disambiguationData":[TD([[makeQuery(id+"F4.imprint","IMPRINT",EDGE,{"derivedFrom":sQuery(id+"F4.wireOp",EDGE,"E8.9.6.0")}),1.0]])]});
            var Q124;
            Q124=makeQuery(id+"F4.imprint","IMPRINT",FACE,{"disambiguationData":[TD([[makeQuery(id+"F4.imprint","IMPRINT",EDGE,{"derivedFrom":sQuery(id+"F4.wireOp",EDGE,"E8.10.0.0")}),1.0]])]});
            var Q125;
            Q125=makeQuery(id+"F4.imprint","IMPRINT",FACE,{"disambiguationData":[TD([[makeQuery(id+"F4.imprint","IMPRINT",EDGE,{"derivedFrom":sQuery(id+"F4.wireOp",EDGE,"E8.10.1.0")}),1.0]])]});
            var Q126;
            Q126=makeQuery(id+"F4.imprint","IMPRINT",FACE,{"disambiguationData":[TD([[makeQuery(id+"F4.imprint","IMPRINT",EDGE,{"derivedFrom":sQuery(id+"F4.wireOp",EDGE,"E8.10.2.0")}),1.0]])]});
            var Q127;
            Q127=makeQuery(id+"F4.imprint","IMPRINT",FACE,{"disambiguationData":[TD([[makeQuery(id+"F4.imprint","IMPRINT",EDGE,{"derivedFrom":sQuery(id+"F4.wireOp",EDGE,"E8.10.3.0")}),1.0]])]});
            var Q128;
            Q128=makeQuery(id+"F4.imprint","IMPRINT",FACE,{"disambiguationData":[TD([[makeQuery(id+"F4.imprint","IMPRINT",EDGE,{"derivedFrom":sQuery(id+"F4.wireOp",EDGE,"E8.10.4.0")}),1.0]])]});
            var Q129;
            Q129=makeQuery(id+"F4.imprint","IMPRINT",FACE,{"disambiguationData":[TD([[makeQuery(id+"F4.imprint","IMPRINT",EDGE,{"derivedFrom":sQuery(id+"F4.wireOp",EDGE,"E8.10.5.0")}),1.0]])]});
            var Q130;
            Q130=makeQuery(id+"F4.imprint","IMPRINT",FACE,{"disambiguationData":[TD([[makeQuery(id+"F4.imprint","IMPRINT",EDGE,{"derivedFrom":sQuery(id+"F4.wireOp",EDGE,"E8.10.6.0")}),1.0]])]});
            var Q131;
            Q131=makeQuery(id+"F4.imprint","IMPRINT",FACE,{"disambiguationData":[TD([[makeQuery(id+"F4.imprint","IMPRINT",EDGE,{"derivedFrom":sQuery(id+"F4.wireOp",EDGE,"E8.11.0.0")}),1.0]])]});
            var Q132;
            Q132=makeQuery(id+"F4.imprint","IMPRINT",FACE,{"disambiguationData":[TD([[makeQuery(id+"F4.imprint","IMPRINT",EDGE,{"derivedFrom":sQuery(id+"F4.wireOp",EDGE,"E8.11.1.0")}),1.0]])]});
            var Q133;
            Q133=makeQuery(id+"F4.imprint","IMPRINT",FACE,{"disambiguationData":[TD([[makeQuery(id+"F4.imprint","IMPRINT",EDGE,{"derivedFrom":sQuery(id+"F4.wireOp",EDGE,"E8.11.2.0")}),1.0]])]});
            var Q134;
            Q134=makeQuery(id+"F4.imprint","IMPRINT",FACE,{"disambiguationData":[TD([[makeQuery(id+"F4.imprint","IMPRINT",EDGE,{"derivedFrom":sQuery(id+"F4.wireOp",EDGE,"E8.11.3.0")}),1.0]])]});
            var Q135;
            Q135=makeQuery(id+"F4.imprint","IMPRINT",FACE,{"disambiguationData":[TD([[makeQuery(id+"F4.imprint","IMPRINT",EDGE,{"derivedFrom":sQuery(id+"F4.wireOp",EDGE,"E8.11.4.0")}),1.0]])]});
            var Q136;
            Q136=makeQuery(id+"F4.imprint","IMPRINT",FACE,{"disambiguationData":[TD([[makeQuery(id+"F4.imprint","IMPRINT",EDGE,{"derivedFrom":sQuery(id+"F4.wireOp",EDGE,"E8.11.5.0")}),1.0]])]});
            var Q137;
            Q137=makeQuery(id+"F4.imprint","IMPRINT",FACE,{"disambiguationData":[TD([[makeQuery(id+"F4.imprint","IMPRINT",EDGE,{"derivedFrom":sQuery(id+"F4.wireOp",EDGE,"E8.11.6.0")}),1.0]])]});
            var Q138;
            Q138=makeQuery(id+"F4.imprint","IMPRINT",FACE,{"disambiguationData":[TD([[makeQuery(id+"F4.imprint","IMPRINT",EDGE,{"derivedFrom":sQuery(id+"F4.wireOp",EDGE,"E9.0.1.7")}),1.0]])]});
            var Q139;
            Q139=makeQuery(id+"F4.imprint","IMPRINT",FACE,{"disambiguationData":[TD([[makeQuery(id+"F4.imprint","IMPRINT",EDGE,{"derivedFrom":sQuery(id+"F4.wireOp",EDGE,"E9.0.2.7")}),1.0]])]});
            var Q140;
            Q140=makeQuery(id+"F4.imprint","IMPRINT",FACE,{"disambiguationData":[TD([[makeQuery(id+"F4.imprint","IMPRINT",EDGE,{"derivedFrom":sQuery(id+"F4.wireOp",EDGE,"E9.0.3.7")}),1.0]])]});
            var Q141;
            Q141=makeQuery(id+"F4.imprint","IMPRINT",FACE,{"disambiguationData":[TD([[makeQuery(id+"F4.imprint","IMPRINT",EDGE,{"derivedFrom":sQuery(id+"F4.wireOp",EDGE,"E9.0.4.7")}),1.0]])]});
            var Q142;
            Q142=makeQuery(id+"F4.imprint","IMPRINT",FACE,{"disambiguationData":[TD([[makeQuery(id+"F4.imprint","IMPRINT",EDGE,{"derivedFrom":sQuery(id+"F4.wireOp",EDGE,"E9.0.5.7")}),1.0]])]});
            var Q143;
            Q143=makeQuery(id+"F4.imprint","IMPRINT",FACE,{"disambiguationData":[TD([[makeQuery(id+"F4.imprint","IMPRINT",EDGE,{"derivedFrom":sQuery(id+"F4.wireOp",EDGE,"E9.0.6.7")}),1.0]])]});
            var Q144;
            Q144=makeQuery(id+"F4.imprint","IMPRINT",FACE,{"disambiguationData":[TD([[makeQuery(id+"F4.imprint","IMPRINT",EDGE,{"derivedFrom":sQuery(id+"F4.wireOp",EDGE,"E9.0.7.7")}),1.0]])]});
            var Q145;
            Q145=makeQuery(id+"F4.imprint","IMPRINT",FACE,{"disambiguationData":[TD([[makeQuery(id+"F4.imprint","IMPRINT",EDGE,{"derivedFrom":sQuery(id+"F4.wireOp",EDGE,"E9.0.8.7")}),1.0]])]});
            var Q146;
            Q146=makeQuery(id+"F4.imprint","IMPRINT",FACE,{"disambiguationData":[TD([[makeQuery(id+"F4.imprint","IMPRINT",EDGE,{"derivedFrom":sQuery(id+"F4.wireOp",EDGE,"E9.0.9.7")}),1.0]])]});
            var Q147;
            Q147=makeQuery(id+"F4.imprint","IMPRINT",FACE,{"disambiguationData":[TD([[makeQuery(id+"F4.imprint","IMPRINT",EDGE,{"derivedFrom":sQuery(id+"F4.wireOp",EDGE,"E10.0.10.1")}),1.0]])]});
            var Q148;
            Q148=makeQuery(id+"F4.imprint","IMPRINT",FACE,{"disambiguationData":[TD([[makeQuery(id+"F4.imprint","IMPRINT",EDGE,{"derivedFrom":sQuery(id+"F4.wireOp",EDGE,"E10.0.10.2")}),1.0]])]});
            var Q149;
            Q149=makeQuery(id+"F4.imprint","IMPRINT",FACE,{"disambiguationData":[TD([[makeQuery(id+"F4.imprint","IMPRINT",EDGE,{"derivedFrom":sQuery(id+"F4.wireOp",EDGE,"E10.0.10.3")}),1.0]])]});
            var Q150;
            Q150=makeQuery(id+"F4.imprint","IMPRINT",FACE,{"disambiguationData":[TD([[makeQuery(id+"F4.imprint","IMPRINT",EDGE,{"derivedFrom":sQuery(id+"F4.wireOp",EDGE,"E10.0.10.4")}),1.0]])]});
            var Q151;
            Q151=makeQuery(id+"F4.imprint","IMPRINT",FACE,{"disambiguationData":[TD([[makeQuery(id+"F4.imprint","IMPRINT",EDGE,{"derivedFrom":sQuery(id+"F4.wireOp",EDGE,"E10.0.10.5")}),1.0]])]});
            var Q152;
            Q152=makeQuery(id+"F4.imprint","IMPRINT",FACE,{"disambiguationData":[TD([[makeQuery(id+"F4.imprint","IMPRINT",EDGE,{"derivedFrom":sQuery(id+"F4.wireOp",EDGE,"E10.0.10.6")}),1.0]])]});
            var Q153;
            Q153=makeQuery(id+"F4.imprint","IMPRINT",FACE,{"disambiguationData":[TD([[makeQuery(id+"F4.imprint","IMPRINT",EDGE,{"derivedFrom":sQuery(id+"F4.wireOp",EDGE,"E10.0.10.7")}),1.0]])]});
            var Q154;
            Q154=makeQuery(id+"F4.imprint","IMPRINT",FACE,{"disambiguationData":[TD([[makeQuery(id+"F4.imprint","IMPRINT",EDGE,{"derivedFrom":sQuery(id+"F4.wireOp",EDGE,"E10.0.11.1")}),1.0]])]});
            var Q155;
            Q155=makeQuery(id+"F4.imprint","IMPRINT",FACE,{"disambiguationData":[TD([[makeQuery(id+"F4.imprint","IMPRINT",EDGE,{"derivedFrom":sQuery(id+"F4.wireOp",EDGE,"E10.0.11.2")}),1.0]])]});
            var Q156;
            Q156=makeQuery(id+"F4.imprint","IMPRINT",FACE,{"disambiguationData":[TD([[makeQuery(id+"F4.imprint","IMPRINT",EDGE,{"derivedFrom":sQuery(id+"F4.wireOp",EDGE,"E10.0.11.3")}),1.0]])]});
            var Q157;
            Q157=makeQuery(id+"F4.imprint","IMPRINT",FACE,{"disambiguationData":[TD([[makeQuery(id+"F4.imprint","IMPRINT",EDGE,{"derivedFrom":sQuery(id+"F4.wireOp",EDGE,"E10.0.11.4")}),1.0]])]});
            var Q158;
            Q158=makeQuery(id+"F4.imprint","IMPRINT",FACE,{"disambiguationData":[TD([[makeQuery(id+"F4.imprint","IMPRINT",EDGE,{"derivedFrom":sQuery(id+"F4.wireOp",EDGE,"E10.0.11.5")}),1.0]])]});
            var Q159;
            Q159=makeQuery(id+"F4.imprint","IMPRINT",FACE,{"disambiguationData":[TD([[makeQuery(id+"F4.imprint","IMPRINT",EDGE,{"derivedFrom":sQuery(id+"F4.wireOp",EDGE,"E10.0.11.6")}),1.0]])]});
            var Q160;
            Q160=makeQuery(id+"F4.imprint","IMPRINT",FACE,{"disambiguationData":[TD([[makeQuery(id+"F4.imprint","IMPRINT",EDGE,{"derivedFrom":sQuery(id+"F4.wireOp",EDGE,"E10.0.11.7")}),1.0]])]});
            var Q161;
            {var subQ0=sQuery(id+"F4.wireOp",EDGE,"E7.0.1.0");var subQ1=makeQuery(id+"F1.opExtrude","CAP_EDGE",EDGE,{"disambiguationData":[OSD([sQuery(id+"F0.wireOp",EDGE,"E0.right")])],"isStart":false});var subQ2=makeQuery(id+"F4.imprint","INTERSECT",VERTEX,{"disambiguationData":[OD(0.0)],"derivedFrom":[subQ1,subQ0]});Q161=makeQuery(id+"F4.imprint","IMPRINT",FACE,{"disambiguationData":[TD([[makeQuery(id+"F4.imprint","IMPRINT",EDGE,{"disambiguationData":[TD([[subQ2,1.0]])],"derivedFrom":subQ0}),1.0]])]});}
            var Q162;
            {var subQ0=sQuery(id+"F4.wireOp",EDGE,"E7.0.2.0");var subQ1=makeQuery(id+"F1.opExtrude","CAP_EDGE",EDGE,{"disambiguationData":[OSD([sQuery(id+"F0.wireOp",EDGE,"E0.right")])],"isStart":false});var subQ2=makeQuery(id+"F4.imprint","INTERSECT",VERTEX,{"disambiguationData":[OD(0.0)],"derivedFrom":[subQ1,subQ0]});Q162=makeQuery(id+"F4.imprint","IMPRINT",FACE,{"disambiguationData":[TD([[makeQuery(id+"F4.imprint","IMPRINT",EDGE,{"disambiguationData":[TD([[subQ2,1.0]])],"derivedFrom":subQ0}),1.0]])]});}
            var Q163;
            {var subQ0=sQuery(id+"F4.wireOp",EDGE,"E7.0.3.0");var subQ1=makeQuery(id+"F1.opExtrude","CAP_EDGE",EDGE,{"disambiguationData":[OSD([sQuery(id+"F0.wireOp",EDGE,"E0.right")])],"isStart":false});var subQ2=makeQuery(id+"F4.imprint","INTERSECT",VERTEX,{"disambiguationData":[OD(0.0)],"derivedFrom":[subQ1,subQ0]});Q163=makeQuery(id+"F4.imprint","IMPRINT",FACE,{"disambiguationData":[TD([[makeQuery(id+"F4.imprint","IMPRINT",EDGE,{"disambiguationData":[TD([[subQ2,1.0]])],"derivedFrom":subQ0}),1.0]])]});}
            var Q164;
            {var subQ0=sQuery(id+"F4.wireOp",EDGE,"E7.0.4.0");var subQ1=makeQuery(id+"F1.opExtrude","CAP_EDGE",EDGE,{"disambiguationData":[OSD([sQuery(id+"F0.wireOp",EDGE,"E0.right")])],"isStart":false});var subQ2=makeQuery(id+"F4.imprint","INTERSECT",VERTEX,{"disambiguationData":[OD(0.0)],"derivedFrom":[subQ1,subQ0]});Q164=makeQuery(id+"F4.imprint","IMPRINT",FACE,{"disambiguationData":[TD([[makeQuery(id+"F4.imprint","IMPRINT",EDGE,{"disambiguationData":[TD([[subQ2,-1.0]])],"derivedFrom":subQ0}),1.0]])]});}
            var Q165;
            {var subQ0=sQuery(id+"F4.wireOp",EDGE,"E7.0.5.0");var subQ1=makeQuery(id+"F1.opExtrude","CAP_EDGE",EDGE,{"disambiguationData":[OSD([sQuery(id+"F0.wireOp",EDGE,"E0.right")])],"isStart":false});var subQ2=makeQuery(id+"F4.imprint","INTERSECT",VERTEX,{"disambiguationData":[OD(0.0)],"derivedFrom":[subQ1,subQ0]});Q165=makeQuery(id+"F4.imprint","IMPRINT",FACE,{"disambiguationData":[TD([[makeQuery(id+"F4.imprint","IMPRINT",EDGE,{"disambiguationData":[TD([[subQ2,-1.0]])],"derivedFrom":subQ0}),1.0]])]});}
            var Q166;
            {var subQ0=sQuery(id+"F4.wireOp",EDGE,"E7.0.6.0");var subQ1=makeQuery(id+"F1.opExtrude","CAP_EDGE",EDGE,{"disambiguationData":[OSD([sQuery(id+"F0.wireOp",EDGE,"E0.right")])],"isStart":false});var subQ2=makeQuery(id+"F4.imprint","INTERSECT",VERTEX,{"disambiguationData":[OD(0.0)],"derivedFrom":[subQ1,subQ0]});Q166=makeQuery(id+"F4.imprint","IMPRINT",FACE,{"disambiguationData":[TD([[makeQuery(id+"F4.imprint","IMPRINT",EDGE,{"disambiguationData":[TD([[subQ2,-1.0]])],"derivedFrom":subQ0}),1.0]])]});}
            var Q167;
            {var subQ0=sQuery(id+"F4.wireOp",EDGE,"E7.1.0.0");var subQ1=makeQuery(id+"F1.opExtrude","CAP_EDGE",EDGE,{"disambiguationData":[OSD([sQuery(id+"F0.wireOp",EDGE,"E0.top")])],"isStart":false});var subQ2=makeQuery(id+"F4.imprint","INTERSECT",VERTEX,{"disambiguationData":[OD(0.0)],"derivedFrom":[subQ1,subQ0]});Q167=makeQuery(id+"F4.imprint","IMPRINT",FACE,{"disambiguationData":[TD([[makeQuery(id+"F4.imprint","IMPRINT",EDGE,{"disambiguationData":[TD([[subQ2,-1.0]])],"derivedFrom":subQ0}),1.0]])]});}
            var Q168;
            {var subQ0=sQuery(id+"F4.wireOp",EDGE,"E7.2.0.0");var subQ1=makeQuery(id+"F1.opExtrude","CAP_EDGE",EDGE,{"disambiguationData":[OSD([sQuery(id+"F0.wireOp",EDGE,"E0.top")])],"isStart":false});var subQ2=makeQuery(id+"F4.imprint","INTERSECT",VERTEX,{"disambiguationData":[OD(0.0)],"derivedFrom":[subQ1,subQ0]});Q168=makeQuery(id+"F4.imprint","IMPRINT",FACE,{"disambiguationData":[TD([[makeQuery(id+"F4.imprint","IMPRINT",EDGE,{"disambiguationData":[TD([[subQ2,-1.0]])],"derivedFrom":subQ0}),1.0]])]});}
            var Q169;
            {var subQ0=sQuery(id+"F4.wireOp",EDGE,"E7.3.0.0");var subQ1=makeQuery(id+"F1.opExtrude","CAP_EDGE",EDGE,{"disambiguationData":[OSD([sQuery(id+"F0.wireOp",EDGE,"E0.top")])],"isStart":false});var subQ2=makeQuery(id+"F4.imprint","INTERSECT",VERTEX,{"disambiguationData":[OD(0.0)],"derivedFrom":[subQ1,subQ0]});Q169=makeQuery(id+"F4.imprint","IMPRINT",FACE,{"disambiguationData":[TD([[makeQuery(id+"F4.imprint","IMPRINT",EDGE,{"disambiguationData":[TD([[subQ2,-1.0]])],"derivedFrom":subQ0}),1.0]])]});}
            var Q170;
            {var subQ0=sQuery(id+"F4.wireOp",EDGE,"E7.4.0.0");var subQ1=makeQuery(id+"F1.opExtrude","CAP_EDGE",EDGE,{"disambiguationData":[OSD([sQuery(id+"F0.wireOp",EDGE,"E0.top")])],"isStart":false});var subQ2=makeQuery(id+"F4.imprint","INTERSECT",VERTEX,{"disambiguationData":[OD(0.0)],"derivedFrom":[subQ1,subQ0]});Q170=makeQuery(id+"F4.imprint","IMPRINT",FACE,{"disambiguationData":[TD([[makeQuery(id+"F4.imprint","IMPRINT",EDGE,{"disambiguationData":[TD([[subQ2,-1.0]])],"derivedFrom":subQ0}),1.0]])]});}
            var Q171;
            {var subQ0=sQuery(id+"F4.wireOp",EDGE,"E7.5.0.0");var subQ1=makeQuery(id+"F1.opExtrude","CAP_EDGE",EDGE,{"disambiguationData":[OSD([sQuery(id+"F0.wireOp",EDGE,"E0.top")])],"isStart":false});var subQ2=makeQuery(id+"F4.imprint","INTERSECT",VERTEX,{"disambiguationData":[OD(0.0)],"derivedFrom":[subQ1,subQ0]});Q171=makeQuery(id+"F4.imprint","IMPRINT",FACE,{"disambiguationData":[TD([[makeQuery(id+"F4.imprint","IMPRINT",EDGE,{"disambiguationData":[TD([[subQ2,-1.0]])],"derivedFrom":subQ0}),1.0]])]});}
            var Q172;
            {var subQ0=sQuery(id+"F4.wireOp",EDGE,"E7.6.0.0");var subQ1=makeQuery(id+"F1.opExtrude","CAP_EDGE",EDGE,{"disambiguationData":[OSD([sQuery(id+"F0.wireOp",EDGE,"E0.top")])],"isStart":false});var subQ2=makeQuery(id+"F4.imprint","INTERSECT",VERTEX,{"disambiguationData":[OD(0.0)],"derivedFrom":[subQ1,subQ0]});Q172=makeQuery(id+"F4.imprint","IMPRINT",FACE,{"disambiguationData":[TD([[makeQuery(id+"F4.imprint","IMPRINT",EDGE,{"disambiguationData":[TD([[subQ2,-1.0]])],"derivedFrom":subQ0}),1.0]])]});}
            var Q173;
            {var subQ0=sQuery(id+"F4.wireOp",EDGE,"E7.7.0.0");var subQ1=makeQuery(id+"F1.opExtrude","CAP_EDGE",EDGE,{"disambiguationData":[OSD([sQuery(id+"F0.wireOp",EDGE,"E0.top")])],"isStart":false});var subQ2=makeQuery(id+"F4.imprint","INTERSECT",VERTEX,{"disambiguationData":[OD(0.0)],"derivedFrom":[subQ1,subQ0]});Q173=makeQuery(id+"F4.imprint","IMPRINT",FACE,{"disambiguationData":[TD([[makeQuery(id+"F4.imprint","IMPRINT",EDGE,{"disambiguationData":[TD([[subQ2,1.0]])],"derivedFrom":subQ0}),1.0]])]});}
            var Q174;
            {var subQ0=sQuery(id+"F4.wireOp",EDGE,"E7.8.0.0");var subQ1=makeQuery(id+"F1.opExtrude","CAP_EDGE",EDGE,{"disambiguationData":[OSD([sQuery(id+"F0.wireOp",EDGE,"E0.top")])],"isStart":false});var subQ2=makeQuery(id+"F4.imprint","INTERSECT",VERTEX,{"disambiguationData":[OD(0.0)],"derivedFrom":[subQ1,subQ0]});Q174=makeQuery(id+"F4.imprint","IMPRINT",FACE,{"disambiguationData":[TD([[makeQuery(id+"F4.imprint","IMPRINT",EDGE,{"disambiguationData":[TD([[subQ2,1.0]])],"derivedFrom":subQ0}),1.0]])]});}
            var Q175;
            {var subQ0=sQuery(id+"F4.wireOp",EDGE,"E7.9.0.0");var subQ1=makeQuery(id+"F1.opExtrude","CAP_EDGE",EDGE,{"disambiguationData":[OSD([sQuery(id+"F0.wireOp",EDGE,"E0.top")])],"isStart":false});var subQ2=makeQuery(id+"F4.imprint","INTERSECT",VERTEX,{"disambiguationData":[OD(0.0)],"derivedFrom":[subQ1,subQ0]});Q175=makeQuery(id+"F4.imprint","IMPRINT",FACE,{"disambiguationData":[TD([[makeQuery(id+"F4.imprint","IMPRINT",EDGE,{"disambiguationData":[TD([[subQ2,1.0]])],"derivedFrom":subQ0}),1.0]])]});}
            var Q176;
            {var subQ0=sQuery(id+"F4.wireOp",EDGE,"E8.0.7.0");var subQ1=makeQuery(id+"F1.opExtrude","CAP_EDGE",EDGE,{"disambiguationData":[OSD([sQuery(id+"F0.wireOp",EDGE,"E0.bottom")])],"isStart":false});var subQ2=makeQuery(id+"F4.imprint","INTERSECT",VERTEX,{"disambiguationData":[OD(0.0)],"derivedFrom":[subQ1,subQ0]});Q176=makeQuery(id+"F4.imprint","IMPRINT",FACE,{"disambiguationData":[TD([[makeQuery(id+"F4.imprint","IMPRINT",EDGE,{"disambiguationData":[TD([[subQ2,1.0]])],"derivedFrom":subQ0}),1.0]])]});}
            var Q177;
            {var subQ0=sQuery(id+"F4.wireOp",EDGE,"E8.1.7.0");var subQ1=makeQuery(id+"F1.opExtrude","CAP_EDGE",EDGE,{"disambiguationData":[OSD([sQuery(id+"F0.wireOp",EDGE,"E0.bottom")])],"isStart":false});var subQ2=makeQuery(id+"F4.imprint","INTERSECT",VERTEX,{"disambiguationData":[OD(0.0)],"derivedFrom":[subQ1,subQ0]});Q177=makeQuery(id+"F4.imprint","IMPRINT",FACE,{"disambiguationData":[TD([[makeQuery(id+"F4.imprint","IMPRINT",EDGE,{"disambiguationData":[TD([[subQ2,1.0]])],"derivedFrom":subQ0}),1.0]])]});}
            var Q178;
            {var subQ0=sQuery(id+"F4.wireOp",EDGE,"E8.2.7.0");var subQ1=makeQuery(id+"F1.opExtrude","CAP_EDGE",EDGE,{"disambiguationData":[OSD([sQuery(id+"F0.wireOp",EDGE,"E0.bottom")])],"isStart":false});var subQ2=makeQuery(id+"F4.imprint","INTERSECT",VERTEX,{"disambiguationData":[OD(0.0)],"derivedFrom":[subQ1,subQ0]});Q178=makeQuery(id+"F4.imprint","IMPRINT",FACE,{"disambiguationData":[TD([[makeQuery(id+"F4.imprint","IMPRINT",EDGE,{"disambiguationData":[TD([[subQ2,1.0]])],"derivedFrom":subQ0}),1.0]])]});}
            var Q179;
            {var subQ0=sQuery(id+"F4.wireOp",EDGE,"E8.3.7.0");var subQ1=makeQuery(id+"F1.opExtrude","CAP_EDGE",EDGE,{"disambiguationData":[OSD([sQuery(id+"F0.wireOp",EDGE,"E0.bottom")])],"isStart":false});var subQ2=makeQuery(id+"F4.imprint","INTERSECT",VERTEX,{"disambiguationData":[OD(0.0)],"derivedFrom":[subQ1,subQ0]});Q179=makeQuery(id+"F4.imprint","IMPRINT",FACE,{"disambiguationData":[TD([[makeQuery(id+"F4.imprint","IMPRINT",EDGE,{"disambiguationData":[TD([[subQ2,1.0]])],"derivedFrom":subQ0}),1.0]])]});}
            var Q180;
            {var subQ0=sQuery(id+"F4.wireOp",EDGE,"E8.4.7.0");var subQ1=makeQuery(id+"F1.opExtrude","CAP_EDGE",EDGE,{"disambiguationData":[OSD([sQuery(id+"F0.wireOp",EDGE,"E0.bottom")])],"isStart":false});var subQ2=makeQuery(id+"F4.imprint","INTERSECT",VERTEX,{"disambiguationData":[OD(0.0)],"derivedFrom":[subQ1,subQ0]});Q180=makeQuery(id+"F4.imprint","IMPRINT",FACE,{"disambiguationData":[TD([[makeQuery(id+"F4.imprint","IMPRINT",EDGE,{"disambiguationData":[TD([[subQ2,1.0]])],"derivedFrom":subQ0}),1.0]])]});}
            var Q181;
            {var subQ0=sQuery(id+"F4.wireOp",EDGE,"E8.5.7.0");var subQ1=makeQuery(id+"F1.opExtrude","CAP_EDGE",EDGE,{"disambiguationData":[OSD([sQuery(id+"F0.wireOp",EDGE,"E0.bottom")])],"isStart":false});var subQ2=makeQuery(id+"F4.imprint","INTERSECT",VERTEX,{"disambiguationData":[OD(0.0)],"derivedFrom":[subQ1,subQ0]});Q181=makeQuery(id+"F4.imprint","IMPRINT",FACE,{"disambiguationData":[TD([[makeQuery(id+"F4.imprint","IMPRINT",EDGE,{"disambiguationData":[TD([[subQ2,1.0]])],"derivedFrom":subQ0}),1.0]])]});}
            var Q182;
            {var subQ0=sQuery(id+"F4.wireOp",EDGE,"E8.6.7.0");var subQ1=makeQuery(id+"F1.opExtrude","CAP_EDGE",EDGE,{"disambiguationData":[OSD([sQuery(id+"F0.wireOp",EDGE,"E0.bottom")])],"isStart":false});var subQ2=makeQuery(id+"F4.imprint","INTERSECT",VERTEX,{"disambiguationData":[OD(0.0)],"derivedFrom":[subQ1,subQ0]});Q182=makeQuery(id+"F4.imprint","IMPRINT",FACE,{"disambiguationData":[TD([[makeQuery(id+"F4.imprint","IMPRINT",EDGE,{"disambiguationData":[TD([[subQ2,-1.0]])],"derivedFrom":subQ0}),1.0]])]});}
            var Q183;
            {var subQ0=sQuery(id+"F4.wireOp",EDGE,"E8.7.7.0");var subQ1=makeQuery(id+"F1.opExtrude","CAP_EDGE",EDGE,{"disambiguationData":[OSD([sQuery(id+"F0.wireOp",EDGE,"E0.bottom")])],"isStart":false});var subQ2=makeQuery(id+"F4.imprint","INTERSECT",VERTEX,{"disambiguationData":[OD(0.0)],"derivedFrom":[subQ1,subQ0]});Q183=makeQuery(id+"F4.imprint","IMPRINT",FACE,{"disambiguationData":[TD([[makeQuery(id+"F4.imprint","IMPRINT",EDGE,{"disambiguationData":[TD([[subQ2,-1.0]])],"derivedFrom":subQ0}),1.0]])]});}
            var Q184;
            {var subQ0=sQuery(id+"F4.wireOp",EDGE,"E8.8.7.0");var subQ1=makeQuery(id+"F1.opExtrude","CAP_EDGE",EDGE,{"disambiguationData":[OSD([sQuery(id+"F0.wireOp",EDGE,"E0.bottom")])],"isStart":false});var subQ2=makeQuery(id+"F4.imprint","INTERSECT",VERTEX,{"disambiguationData":[OD(0.0)],"derivedFrom":[subQ1,subQ0]});Q184=makeQuery(id+"F4.imprint","IMPRINT",FACE,{"disambiguationData":[TD([[makeQuery(id+"F4.imprint","IMPRINT",EDGE,{"disambiguationData":[TD([[subQ2,-1.0]])],"derivedFrom":subQ0}),1.0]])]});}
            var Q185;
            {var subQ0=sQuery(id+"F4.wireOp",EDGE,"E8.9.7.0");var subQ1=makeQuery(id+"F1.opExtrude","CAP_EDGE",EDGE,{"disambiguationData":[OSD([sQuery(id+"F0.wireOp",EDGE,"E0.bottom")])],"isStart":false});var subQ2=makeQuery(id+"F4.imprint","INTERSECT",VERTEX,{"disambiguationData":[OD(0.0)],"derivedFrom":[subQ1,subQ0]});Q185=makeQuery(id+"F4.imprint","IMPRINT",FACE,{"disambiguationData":[TD([[makeQuery(id+"F4.imprint","IMPRINT",EDGE,{"disambiguationData":[TD([[subQ2,-1.0]])],"derivedFrom":subQ0}),1.0]])]});}
            var Q186;
            {var subQ0=sQuery(id+"F4.wireOp",EDGE,"E8.10.7.0");var subQ1=makeQuery(id+"F1.opExtrude","CAP_EDGE",EDGE,{"disambiguationData":[OSD([sQuery(id+"F0.wireOp",EDGE,"E0.bottom")])],"isStart":false});var subQ2=makeQuery(id+"F4.imprint","INTERSECT",VERTEX,{"disambiguationData":[OD(0.0)],"derivedFrom":[subQ1,subQ0]});Q186=makeQuery(id+"F4.imprint","IMPRINT",FACE,{"disambiguationData":[TD([[makeQuery(id+"F4.imprint","IMPRINT",EDGE,{"disambiguationData":[TD([[subQ2,-1.0]])],"derivedFrom":subQ0}),1.0]])]});}
            var Q187;
            {var subQ0=sQuery(id+"F4.wireOp",EDGE,"E8.11.7.0");var subQ1=makeQuery(id+"F1.opExtrude","CAP_EDGE",EDGE,{"disambiguationData":[OSD([sQuery(id+"F0.wireOp",EDGE,"E0.bottom")])],"isStart":false});var subQ2=makeQuery(id+"F4.imprint","INTERSECT",VERTEX,{"disambiguationData":[OD(0.0)],"derivedFrom":[subQ1,subQ0]});Q187=makeQuery(id+"F4.imprint","IMPRINT",FACE,{"disambiguationData":[TD([[makeQuery(id+"F4.imprint","IMPRINT",EDGE,{"disambiguationData":[TD([[subQ2,-1.0]])],"derivedFrom":subQ0}),1.0]])]});}
            var Q188;
            {var subQ0=sQuery(id+"F4.wireOp",EDGE,"E9.0.0.7");var subQ1=makeQuery(id+"F1.opExtrude","CAP_EDGE",EDGE,{"disambiguationData":[OSD([sQuery(id+"F0.wireOp",EDGE,"E0.right")])],"isStart":false});var subQ2=makeQuery(id+"F4.imprint","INTERSECT",VERTEX,{"disambiguationData":[OD(0.0)],"derivedFrom":[subQ1,subQ0]});Q188=makeQuery(id+"F4.imprint","IMPRINT",FACE,{"disambiguationData":[TD([[makeQuery(id+"F4.imprint","IMPRINT",EDGE,{"disambiguationData":[TD([[subQ2,-1.0]])],"derivedFrom":subQ0}),1.0]])]});}
            var Q189;
            {var subQ0=sQuery(id+"F4.wireOp",EDGE,"E10.0.10.0");var subQ1=makeQuery(id+"F1.opExtrude","CAP_EDGE",EDGE,{"disambiguationData":[OSD([sQuery(id+"F0.wireOp",EDGE,"E0.top")])],"isStart":false});var subQ2=makeQuery(id+"F4.imprint","INTERSECT",VERTEX,{"disambiguationData":[OD(0.0)],"derivedFrom":[subQ1,subQ0]});Q189=makeQuery(id+"F4.imprint","IMPRINT",FACE,{"disambiguationData":[TD([[makeQuery(id+"F4.imprint","IMPRINT",EDGE,{"disambiguationData":[TD([[subQ2,1.0]])],"derivedFrom":subQ0}),1.0]])]});}
            var Q190;
            {var subQ0=sQuery(id+"F4.wireOp",EDGE,"E10.0.11.0");var subQ1=makeQuery(id+"F1.opExtrude","CAP_EDGE",EDGE,{"disambiguationData":[OSD([sQuery(id+"F0.wireOp",EDGE,"E0.top")])],"isStart":false});var subQ2=makeQuery(id+"F4.imprint","INTERSECT",VERTEX,{"disambiguationData":[OD(0.0)],"derivedFrom":[subQ1,subQ0]});Q190=makeQuery(id+"F4.imprint","IMPRINT",FACE,{"disambiguationData":[TD([[makeQuery(id+"F4.imprint","IMPRINT",EDGE,{"disambiguationData":[TD([[subQ2,1.0]])],"derivedFrom":subQ0}),1.0]])]});}
            var Q191;
            {var subQ0=sQuery(id+"F4.wireOp",EDGE,"E11.0.12.1");var subQ1=makeQuery(id+"F1.opExtrude","CAP_EDGE",EDGE,{"disambiguationData":[OSD([sQuery(id+"F0.wireOp",EDGE,"E0.left")])],"isStart":false});var subQ2=makeQuery(id+"F4.imprint","INTERSECT",VERTEX,{"disambiguationData":[OD(0.0)],"derivedFrom":[subQ1,subQ0]});Q191=makeQuery(id+"F4.imprint","IMPRINT",FACE,{"disambiguationData":[TD([[makeQuery(id+"F4.imprint","IMPRINT",EDGE,{"disambiguationData":[TD([[subQ2,-1.0]])],"derivedFrom":subQ0}),1.0]])]});}
            var Q192;
            {var subQ0=sQuery(id+"F4.wireOp",EDGE,"E11.0.12.2");var subQ1=makeQuery(id+"F1.opExtrude","CAP_EDGE",EDGE,{"disambiguationData":[OSD([sQuery(id+"F0.wireOp",EDGE,"E0.left")])],"isStart":false});var subQ2=makeQuery(id+"F4.imprint","INTERSECT",VERTEX,{"disambiguationData":[OD(0.0)],"derivedFrom":[subQ1,subQ0]});Q192=makeQuery(id+"F4.imprint","IMPRINT",FACE,{"disambiguationData":[TD([[makeQuery(id+"F4.imprint","IMPRINT",EDGE,{"disambiguationData":[TD([[subQ2,-1.0]])],"derivedFrom":subQ0}),1.0]])]});}
            var Q193;
            {var subQ0=sQuery(id+"F4.wireOp",EDGE,"E11.0.12.3");var subQ1=makeQuery(id+"F1.opExtrude","CAP_EDGE",EDGE,{"disambiguationData":[OSD([sQuery(id+"F0.wireOp",EDGE,"E0.left")])],"isStart":false});var subQ2=makeQuery(id+"F4.imprint","INTERSECT",VERTEX,{"disambiguationData":[OD(0.0)],"derivedFrom":[subQ1,subQ0]});Q193=makeQuery(id+"F4.imprint","IMPRINT",FACE,{"disambiguationData":[TD([[makeQuery(id+"F4.imprint","IMPRINT",EDGE,{"disambiguationData":[TD([[subQ2,-1.0]])],"derivedFrom":subQ0}),1.0]])]});}
            var Q194;
            {var subQ0=sQuery(id+"F4.wireOp",EDGE,"E11.0.12.4");var subQ1=makeQuery(id+"F1.opExtrude","CAP_EDGE",EDGE,{"disambiguationData":[OSD([sQuery(id+"F0.wireOp",EDGE,"E0.left")])],"isStart":false});var subQ2=makeQuery(id+"F4.imprint","INTERSECT",VERTEX,{"disambiguationData":[OD(0.0)],"derivedFrom":[subQ1,subQ0]});Q194=makeQuery(id+"F4.imprint","IMPRINT",FACE,{"disambiguationData":[TD([[makeQuery(id+"F4.imprint","IMPRINT",EDGE,{"disambiguationData":[TD([[subQ2,1.0]])],"derivedFrom":subQ0}),1.0]])]});}
            var Q195;
            {var subQ0=sQuery(id+"F4.wireOp",EDGE,"E11.0.12.5");var subQ1=makeQuery(id+"F1.opExtrude","CAP_EDGE",EDGE,{"disambiguationData":[OSD([sQuery(id+"F0.wireOp",EDGE,"E0.left")])],"isStart":false});var subQ2=makeQuery(id+"F4.imprint","INTERSECT",VERTEX,{"disambiguationData":[OD(0.0)],"derivedFrom":[subQ1,subQ0]});Q195=makeQuery(id+"F4.imprint","IMPRINT",FACE,{"disambiguationData":[TD([[makeQuery(id+"F4.imprint","IMPRINT",EDGE,{"disambiguationData":[TD([[subQ2,1.0]])],"derivedFrom":subQ0}),1.0]])]});}
            var Q196;
            {var subQ0=sQuery(id+"F4.wireOp",EDGE,"E11.0.12.6");var subQ1=makeQuery(id+"F1.opExtrude","CAP_EDGE",EDGE,{"disambiguationData":[OSD([sQuery(id+"F0.wireOp",EDGE,"E0.left")])],"isStart":false});var subQ2=makeQuery(id+"F4.imprint","INTERSECT",VERTEX,{"disambiguationData":[OD(0.0)],"derivedFrom":[subQ1,subQ0]});Q196=makeQuery(id+"F4.imprint","IMPRINT",FACE,{"disambiguationData":[TD([[makeQuery(id+"F4.imprint","IMPRINT",EDGE,{"disambiguationData":[TD([[subQ2,1.0]])],"derivedFrom":subQ0}),1.0]])]});}
            var Q197;
            {var subQ0=sQuery(id+"F4.wireOp",EDGE,"E11.0.12.7");var subQ1=makeQuery(id+"F1.opExtrude","CAP_EDGE",EDGE,{"disambiguationData":[OSD([sQuery(id+"F0.wireOp",EDGE,"E0.left")])],"isStart":false});var subQ2=makeQuery(id+"F4.imprint","INTERSECT",VERTEX,{"disambiguationData":[OD(0.0)],"derivedFrom":[subQ1,subQ0]});Q197=makeQuery(id+"F4.imprint","IMPRINT",FACE,{"disambiguationData":[TD([[makeQuery(id+"F4.imprint","IMPRINT",EDGE,{"disambiguationData":[TD([[subQ2,1.0]])],"derivedFrom":subQ0}),1.0]])]});}
            var Q198;
            {var subQ0=sQuery(id+"F4.wireOp",EDGE,"E5");var subQ1=makeQuery(id+"F1.opExtrude","CAP_EDGE",EDGE,{"disambiguationData":[OSD([sQuery(id+"F0.wireOp",EDGE,"E0.top")])],"isStart":false});var subQ2=makeQuery(id+"F4.imprint","INTERSECT",VERTEX,{"derivedFrom":[subQ1,subQ0]});Q198=makeQuery(id+"F4.imprint","IMPRINT",FACE,{"disambiguationData":[TD([[makeQuery(id+"F4.imprint","IMPRINT",EDGE,{"disambiguationData":[TD([[subQ2,1.0]])],"derivedFrom":subQ0}),1.0]])]});}
            var Q199;
            {var subQ0=sQuery(id+"F4.wireOp",EDGE,"E11.0.12.0");var subQ1=makeQuery(id+"F1.opExtrude","CAP_EDGE",EDGE,{"disambiguationData":[OSD([sQuery(id+"F0.wireOp",EDGE,"E0.top")])],"isStart":false});var subQ2=makeQuery(id+"F4.imprint","INTERSECT",VERTEX,{"derivedFrom":[subQ1,subQ0]});Q199=makeQuery(id+"F4.imprint","IMPRINT",FACE,{"disambiguationData":[TD([[makeQuery(id+"F4.imprint","IMPRINT",EDGE,{"disambiguationData":[TD([[subQ2,-1.0]])],"derivedFrom":subQ0}),1.0]])]});}
            extrude(context, id + "F5", {"entities" : qUnion([Q0, Q1, Q2, Q3, Q4, Q5, Q6, Q7, Q8, Q9, Q10, Q11, Q12, Q13, Q14, Q15, Q16, Q17, Q18, Q19, Q20, Q21, Q22, Q23, Q24, Q25, Q26, Q27, Q28, Q29, Q30, Q31, Q32, Q33, Q34, Q35, Q36, Q37, Q38, Q39, Q40, Q41, Q42, Q43, Q44, Q45, Q46, Q47, Q48, Q49, Q50, Q51, Q52, Q53, Q54, Q55, Q56, Q57, Q58, Q59, Q60, Q61, Q62, Q63, Q64, Q65, Q66, Q67, Q68, Q69, Q70, Q71, Q72, Q73, Q74, Q75, Q76, Q77, Q78, Q79, Q80, Q81, Q82, Q83, Q84, Q85, Q86, Q87, Q88, Q89, Q90, Q91, Q92, Q93, Q94, Q95, Q96, Q97, Q98, Q99, Q100, Q101, Q102, Q103, Q104, Q105, Q106, Q107, Q108, Q109, Q110, Q111, Q112, Q113, Q114, Q115, Q116, Q117, Q118, Q119, Q120, Q121, Q122, Q123, Q124, Q125, Q126, Q127, Q128, Q129, Q130, Q131, Q132, Q133, Q134, Q135, Q136, Q137, Q138, Q139, Q140, Q141, Q142, Q143, Q144, Q145, Q146, Q147, Q148, Q149, Q150, Q151, Q152, Q153, Q154, Q155, Q156, Q157, Q158, Q159, Q160, Q161, Q162, Q163, Q164, Q165, Q166, Q167, Q168, Q169, Q170, Q171, Q172, Q173, Q174, Q175, Q176, Q177, Q178, Q179, Q180, Q181, Q182, Q183, Q184, Q185, Q186, Q187, Q188, Q189, Q190, Q191, Q192, Q193, Q194, Q195, Q196, Q197, Q198, Q199]), "operationType" : NewBodyOperationType.ADD, "depth" : 10 * mm, "offsetDistance" : 25 * mm});
        }
    });
